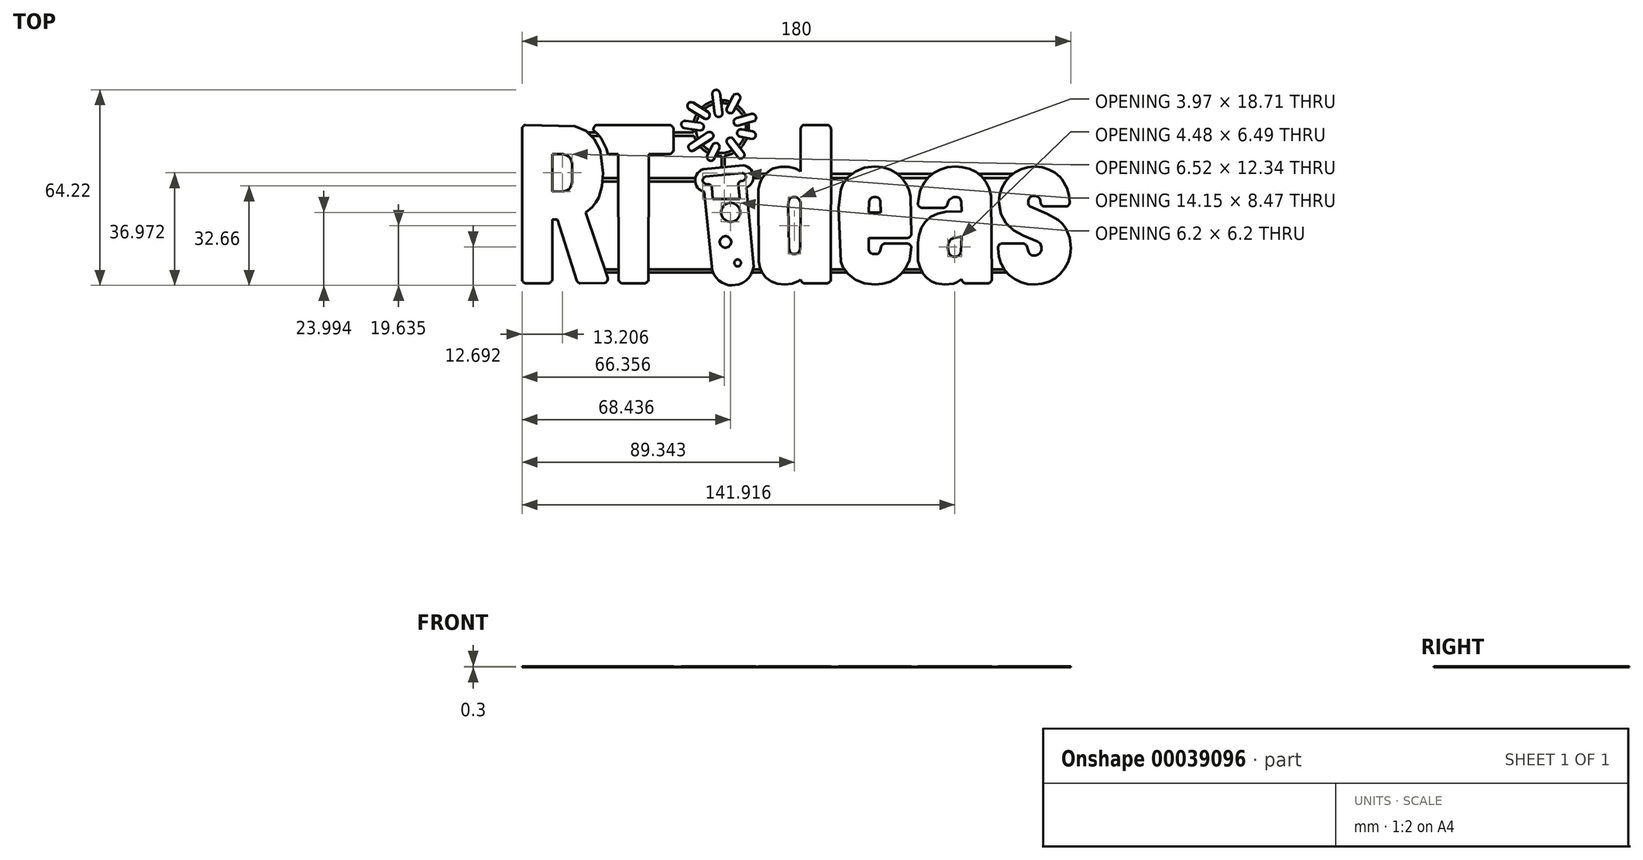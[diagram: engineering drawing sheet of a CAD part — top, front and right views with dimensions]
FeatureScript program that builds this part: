
annotation { "Feature Type Name" : "Feature", "Feature Type Description" : "" }
export const myFeature = defineFeature(function(context is Context, id is Id, definition is map)
    precondition{}
    {
        {
            var Q0;
            Q0=qCreatedBy(makeId("Top.planeOp"),FACE);
            var sketch = newSketch(context, id + "F0", { "sketchPlane" : qUnion([Q0])});
            skLineSegment(sketch, "E0", {"start": v(-21.05, -32.1) * mm, "end": v(-22.22, -32) * mm});
            skLineSegment(sketch, "E1", {"start": v(-22.22, -32) * mm, "end": v(-23.33, -31.71) * mm});
            skLineSegment(sketch, "E2", {"start": v(-23.33, -31.71) * mm, "end": v(-24.38, -31.22) * mm});
            skLineSegment(sketch, "E3", {"start": v(-24.38, -31.22) * mm, "end": v(-25.36, -30.53) * mm});
            skLineSegment(sketch, "E4", {"start": v(-25.36, -30.53) * mm, "end": v(-26.34, -29.57) * mm});
            skLineSegment(sketch, "E5", {"start": v(-26.34, -29.57) * mm, "end": v(-27.07, -28.47) * mm});
            skLineSegment(sketch, "E6", {"start": v(-27.07, -28.47) * mm, "end": v(-27.57, -27.24) * mm});
            skLineSegment(sketch, "E7", {"start": v(-27.57, -27.24) * mm, "end": v(-30.18, -1.33) * mm});
            skLineSegment(sketch, "E8", {"start": v(-30.18, -1.33) * mm, "end": v(-31.06, -1.04) * mm});
            skLineSegment(sketch, "E9", {"start": v(-31.06, -1.04) * mm, "end": v(-31.86, -0.53) * mm});
            skLineSegment(sketch, "E10", {"start": v(-31.86, -0.53) * mm, "end": v(-32.4, 0) * mm});
            skLineSegment(sketch, "E11", {"start": v(-32.4, 0) * mm, "end": v(-32.8, 0.61) * mm});
            skLineSegment(sketch, "E12", {"start": v(-32.8, 0.61) * mm, "end": v(-33.07, 1.3) * mm});
            skLineSegment(sketch, "E13", {"start": v(-33.07, 1.3) * mm, "end": v(-33.22, 2.03) * mm});
            skLineSegment(sketch, "E14", {"start": v(-33.22, 2.03) * mm, "end": v(-33.22, 2.79) * mm});
            skLineSegment(sketch, "E15", {"start": v(-33.22, 2.79) * mm, "end": v(-33.08, 3.5) * mm});
            skLineSegment(sketch, "E16", {"start": v(-33.08, 3.5) * mm, "end": v(-32.8, 4.18) * mm});
            skLineSegment(sketch, "E17", {"start": v(-32.8, 4.18) * mm, "end": v(-32.37, 4.8) * mm});
            skLineSegment(sketch, "E18", {"start": v(-32.37, 4.8) * mm, "end": v(-31.84, 5.34) * mm});
            skLineSegment(sketch, "E19", {"start": v(-31.84, 5.34) * mm, "end": v(-31.22, 5.75) * mm});
            skLineSegment(sketch, "E20", {"start": v(-31.22, 5.75) * mm, "end": v(-30.54, 6.03) * mm});
            skLineSegment(sketch, "E21", {"start": v(-30.54, 6.03) * mm, "end": v(-17.45, 7.28) * mm});
            skLineSegment(sketch, "E22", {"start": v(-17.45, 7.28) * mm, "end": v(-16.73, 7.14) * mm});
            skLineSegment(sketch, "E23", {"start": v(-16.73, 7.14) * mm, "end": v(-16.06, 6.86) * mm});
            skLineSegment(sketch, "E24", {"start": v(-16.06, 6.86) * mm, "end": v(-15.43, 6.44) * mm});
            skLineSegment(sketch, "E25", {"start": v(-15.43, 6.44) * mm, "end": v(-14.9, 5.9) * mm});
            skLineSegment(sketch, "E26", {"start": v(-14.9, 5.9) * mm, "end": v(-14.5, 5.3) * mm});
            skLineSegment(sketch, "E27", {"start": v(-14.5, 5.3) * mm, "end": v(-14.21, 4.61) * mm});
            skLineSegment(sketch, "E28", {"start": v(-14.21, 4.61) * mm, "end": v(-14.07, 3.87) * mm});
            skLineSegment(sketch, "E29", {"start": v(-14.07, 3.87) * mm, "end": v(-14.07, 3.12) * mm});
            skLineSegment(sketch, "E30", {"start": v(-14.07, 3.12) * mm, "end": v(-14.22, 2.4) * mm});
            skLineSegment(sketch, "E31", {"start": v(-14.22, 2.4) * mm, "end": v(-14.5, 1.72) * mm});
            skLineSegment(sketch, "E32", {"start": v(-14.5, 1.72) * mm, "end": v(-15.25, 0.75) * mm});
            skLineSegment(sketch, "E33", {"start": v(-15.25, 0.75) * mm, "end": v(-16, 0.2) * mm});
            skLineSegment(sketch, "E34", {"start": v(-16, 0.2) * mm, "end": v(-16.4, 0) * mm});
            skLineSegment(sketch, "E35", {"start": v(-16.4, 0) * mm, "end": v(-14.05, -25.94) * mm});
            skLineSegment(sketch, "E36", {"start": v(-14.05, -25.94) * mm, "end": v(-14.3, -27.24) * mm});
            skLineSegment(sketch, "E37", {"start": v(-14.3, -27.24) * mm, "end": v(-14.82, -28.46) * mm});
            skLineSegment(sketch, "E38", {"start": v(-14.82, -28.46) * mm, "end": v(-15.6, -29.6) * mm});
            skLineSegment(sketch, "E39", {"start": v(-15.6, -29.6) * mm, "end": v(-16.56, -30.57) * mm});
            skLineSegment(sketch, "E40", {"start": v(-16.56, -30.57) * mm, "end": v(-17.66, -31.31) * mm});
            skLineSegment(sketch, "E41", {"start": v(-17.66, -31.31) * mm, "end": v(-18.89, -31.8) * mm});
            skLineSegment(sketch, "E42", {"start": v(-18.89, -31.8) * mm, "end": v(-21.05, -32.1) * mm});
            skLineSegment(sketch, "E43", {"start": v(-18.14, -24.6) * mm, "end": v(-18.18, -24.38) * mm});
            skLineSegment(sketch, "E44", {"start": v(-18.18, -24.38) * mm, "end": v(-18.26, -24.18) * mm});
            skLineSegment(sketch, "E45", {"start": v(-18.26, -24.18) * mm, "end": v(-18.38, -24) * mm});
            skLineSegment(sketch, "E46", {"start": v(-18.38, -24) * mm, "end": v(-18.54, -23.84) * mm});
            skLineSegment(sketch, "E47", {"start": v(-18.54, -23.84) * mm, "end": v(-18.73, -23.71) * mm});
            skLineSegment(sketch, "E48", {"start": v(-18.73, -23.71) * mm, "end": v(-18.93, -23.63) * mm});
            skLineSegment(sketch, "E49", {"start": v(-18.93, -23.63) * mm, "end": v(-19.15, -23.59) * mm});
            skLineSegment(sketch, "E50", {"start": v(-19.15, -23.59) * mm, "end": v(-19.37, -23.59) * mm});
            skLineSegment(sketch, "E51", {"start": v(-19.37, -23.59) * mm, "end": v(-19.6, -23.63) * mm});
            skLineSegment(sketch, "E52", {"start": v(-19.6, -23.63) * mm, "end": v(-19.8, -23.71) * mm});
            skLineSegment(sketch, "E53", {"start": v(-19.8, -23.71) * mm, "end": v(-19.98, -23.83) * mm});
            skLineSegment(sketch, "E54", {"start": v(-19.98, -23.83) * mm, "end": v(-20.14, -24) * mm});
            skLineSegment(sketch, "E55", {"start": v(-20.14, -24) * mm, "end": v(-20.26, -24.18) * mm});
            skLineSegment(sketch, "E56", {"start": v(-20.26, -24.18) * mm, "end": v(-20.35, -24.38) * mm});
            skLineSegment(sketch, "E57", {"start": v(-20.35, -24.38) * mm, "end": v(-20.39, -24.6) * mm});
            skLineSegment(sketch, "E58", {"start": v(-20.39, -24.6) * mm, "end": v(-20.39, -24.82) * mm});
            skLineSegment(sketch, "E59", {"start": v(-20.39, -24.82) * mm, "end": v(-20.35, -25.04) * mm});
            skLineSegment(sketch, "E60", {"start": v(-20.35, -25.04) * mm, "end": v(-20.27, -25.24) * mm});
            skLineSegment(sketch, "E61", {"start": v(-20.27, -25.24) * mm, "end": v(-20.14, -25.43) * mm});
            skLineSegment(sketch, "E62", {"start": v(-20.14, -25.43) * mm, "end": v(-19.98, -25.58) * mm});
            skLineSegment(sketch, "E63", {"start": v(-19.98, -25.58) * mm, "end": v(-19.8, -25.71) * mm});
            skLineSegment(sketch, "E64", {"start": v(-19.8, -25.71) * mm, "end": v(-19.6, -25.8) * mm});
            skLineSegment(sketch, "E65", {"start": v(-19.6, -25.8) * mm, "end": v(-19.38, -25.84) * mm});
            skLineSegment(sketch, "E66", {"start": v(-19.38, -25.84) * mm, "end": v(-19.16, -25.84) * mm});
            skLineSegment(sketch, "E67", {"start": v(-19.16, -25.84) * mm, "end": v(-18.93, -25.8) * mm});
            skLineSegment(sketch, "E68", {"start": v(-18.93, -25.8) * mm, "end": v(-18.73, -25.71) * mm});
            skLineSegment(sketch, "E69", {"start": v(-18.73, -25.71) * mm, "end": v(-18.55, -25.6) * mm});
            skLineSegment(sketch, "E70", {"start": v(-18.55, -25.6) * mm, "end": v(-18.4, -25.43) * mm});
            skLineSegment(sketch, "E71", {"start": v(-18.4, -25.43) * mm, "end": v(-18.26, -25.24) * mm});
            skLineSegment(sketch, "E72", {"start": v(-18.26, -25.24) * mm, "end": v(-18.18, -25.04) * mm});
            skLineSegment(sketch, "E73", {"start": v(-18.18, -25.04) * mm, "end": v(-18.14, -24.83) * mm});
            skLineSegment(sketch, "E74", {"start": v(-18.14, -24.83) * mm, "end": v(-18.14, -24.6) * mm});
            skLineSegment(sketch, "E75", {"start": v(-21.4, -17.66) * mm, "end": v(-21.48, -17.3) * mm});
            skLineSegment(sketch, "E76", {"start": v(-21.48, -17.3) * mm, "end": v(-21.61, -16.96) * mm});
            skLineSegment(sketch, "E77", {"start": v(-21.61, -16.96) * mm, "end": v(-21.81, -16.66) * mm});
            skLineSegment(sketch, "E78", {"start": v(-21.81, -16.66) * mm, "end": v(-22.08, -16.4) * mm});
            skLineSegment(sketch, "E79", {"start": v(-22.08, -16.4) * mm, "end": v(-22.39, -16.18) * mm});
            skLineSegment(sketch, "E80", {"start": v(-22.39, -16.18) * mm, "end": v(-22.72, -16.04) * mm});
            skLineSegment(sketch, "E81", {"start": v(-22.72, -16.04) * mm, "end": v(-23.07, -15.97) * mm});
            skLineSegment(sketch, "E82", {"start": v(-23.07, -15.97) * mm, "end": v(-23.45, -15.98) * mm});
            skLineSegment(sketch, "E83", {"start": v(-23.45, -15.98) * mm, "end": v(-23.82, -16.05) * mm});
            skLineSegment(sketch, "E84", {"start": v(-23.82, -16.05) * mm, "end": v(-24.15, -16.18) * mm});
            skLineSegment(sketch, "E85", {"start": v(-24.15, -16.18) * mm, "end": v(-24.45, -16.38) * mm});
            skLineSegment(sketch, "E86", {"start": v(-24.45, -16.38) * mm, "end": v(-24.72, -16.65) * mm});
            skLineSegment(sketch, "E87", {"start": v(-24.72, -16.65) * mm, "end": v(-24.93, -16.96) * mm});
            skLineSegment(sketch, "E88", {"start": v(-24.93, -16.96) * mm, "end": v(-25.07, -17.29) * mm});
            skLineSegment(sketch, "E89", {"start": v(-25.07, -17.29) * mm, "end": v(-25.14, -17.64) * mm});
            skLineSegment(sketch, "E90", {"start": v(-25.14, -17.64) * mm, "end": v(-25.13, -18.02) * mm});
            skLineSegment(sketch, "E91", {"start": v(-25.13, -18.02) * mm, "end": v(-25.07, -18.39) * mm});
            skLineSegment(sketch, "E92", {"start": v(-25.07, -18.39) * mm, "end": v(-24.93, -18.72) * mm});
            skLineSegment(sketch, "E93", {"start": v(-24.93, -18.72) * mm, "end": v(-24.73, -19.02) * mm});
            skLineSegment(sketch, "E94", {"start": v(-24.73, -19.02) * mm, "end": v(-24.46, -19.28) * mm});
            skLineSegment(sketch, "E95", {"start": v(-24.46, -19.28) * mm, "end": v(-24.15, -19.5) * mm});
            skLineSegment(sketch, "E96", {"start": v(-24.15, -19.5) * mm, "end": v(-23.82, -19.64) * mm});
            skLineSegment(sketch, "E97", {"start": v(-23.82, -19.64) * mm, "end": v(-23.47, -19.7) * mm});
            skLineSegment(sketch, "E98", {"start": v(-23.47, -19.7) * mm, "end": v(-23.1, -19.7) * mm});
            skLineSegment(sketch, "E99", {"start": v(-23.1, -19.7) * mm, "end": v(-22.72, -19.63) * mm});
            skLineSegment(sketch, "E100", {"start": v(-22.72, -19.63) * mm, "end": v(-22.39, -19.5) * mm});
            skLineSegment(sketch, "E101", {"start": v(-22.39, -19.5) * mm, "end": v(-22.1, -19.3) * mm});
            skLineSegment(sketch, "E102", {"start": v(-22.1, -19.3) * mm, "end": v(-21.83, -19.03) * mm});
            skLineSegment(sketch, "E103", {"start": v(-21.83, -19.03) * mm, "end": v(-21.62, -18.72) * mm});
            skLineSegment(sketch, "E104", {"start": v(-21.62, -18.72) * mm, "end": v(-21.47, -18.4) * mm});
            skLineSegment(sketch, "E105", {"start": v(-21.47, -18.4) * mm, "end": v(-21.4, -18.04) * mm});
            skLineSegment(sketch, "E106", {"start": v(-21.4, -18.04) * mm, "end": v(-21.4, -17.66) * mm});
            skLineSegment(sketch, "E107", {"start": v(-18.47, -7.82) * mm, "end": v(-18.58, -7.2) * mm});
            skLineSegment(sketch, "E108", {"start": v(-18.58, -7.2) * mm, "end": v(-18.8, -6.65) * mm});
            skLineSegment(sketch, "E109", {"start": v(-18.8, -6.65) * mm, "end": v(-19.14, -6.15) * mm});
            skLineSegment(sketch, "E110", {"start": v(-19.14, -6.15) * mm, "end": v(-19.58, -5.72) * mm});
            skLineSegment(sketch, "E111", {"start": v(-19.58, -5.72) * mm, "end": v(-20.1, -5.36) * mm});
            skLineSegment(sketch, "E112", {"start": v(-20.1, -5.36) * mm, "end": v(-20.65, -5.13) * mm});
            skLineSegment(sketch, "E113", {"start": v(-20.65, -5.13) * mm, "end": v(-21.24, -5.02) * mm});
            skLineSegment(sketch, "E114", {"start": v(-21.24, -5.02) * mm, "end": v(-21.86, -5.02) * mm});
            skLineSegment(sketch, "E115", {"start": v(-21.86, -5.02) * mm, "end": v(-22.47, -5.13) * mm});
            skLineSegment(sketch, "E116", {"start": v(-22.47, -5.13) * mm, "end": v(-23.03, -5.36) * mm});
            skLineSegment(sketch, "E117", {"start": v(-23.03, -5.36) * mm, "end": v(-23.52, -5.7) * mm});
            skLineSegment(sketch, "E118", {"start": v(-23.52, -5.7) * mm, "end": v(-23.96, -6.14) * mm});
            skLineSegment(sketch, "E119", {"start": v(-23.96, -6.14) * mm, "end": v(-24.31, -6.65) * mm});
            skLineSegment(sketch, "E120", {"start": v(-24.31, -6.65) * mm, "end": v(-24.55, -7.2) * mm});
            skLineSegment(sketch, "E121", {"start": v(-24.55, -7.2) * mm, "end": v(-24.66, -7.79) * mm});
            skLineSegment(sketch, "E122", {"start": v(-24.66, -7.79) * mm, "end": v(-24.66, -8.41) * mm});
            skLineSegment(sketch, "E123", {"start": v(-24.66, -8.41) * mm, "end": v(-24.55, -9.02) * mm});
            skLineSegment(sketch, "E124", {"start": v(-24.55, -9.02) * mm, "end": v(-24.32, -9.58) * mm});
            skLineSegment(sketch, "E125", {"start": v(-24.32, -9.58) * mm, "end": v(-23.99, -10.08) * mm});
            skLineSegment(sketch, "E126", {"start": v(-23.99, -10.08) * mm, "end": v(-23.54, -10.52) * mm});
            skLineSegment(sketch, "E127", {"start": v(-23.54, -10.52) * mm, "end": v(-23.03, -10.87) * mm});
            skLineSegment(sketch, "E128", {"start": v(-23.03, -10.87) * mm, "end": v(-22.48, -11.1) * mm});
            skLineSegment(sketch, "E129", {"start": v(-22.48, -11.1) * mm, "end": v(-21.9, -11.21) * mm});
            skLineSegment(sketch, "E130", {"start": v(-21.9, -11.21) * mm, "end": v(-21.27, -11.21) * mm});
            skLineSegment(sketch, "E131", {"start": v(-21.27, -11.21) * mm, "end": v(-20.65, -11.1) * mm});
            skLineSegment(sketch, "E132", {"start": v(-20.65, -11.1) * mm, "end": v(-20.1, -10.87) * mm});
            skLineSegment(sketch, "E133", {"start": v(-20.1, -10.87) * mm, "end": v(-19.6, -10.54) * mm});
            skLineSegment(sketch, "E134", {"start": v(-19.6, -10.54) * mm, "end": v(-19.16, -10.1) * mm});
            skLineSegment(sketch, "E135", {"start": v(-19.16, -10.1) * mm, "end": v(-18.81, -9.58) * mm});
            skLineSegment(sketch, "E136", {"start": v(-18.81, -9.58) * mm, "end": v(-18.58, -9.03) * mm});
            skLineSegment(sketch, "E137", {"start": v(-18.58, -9.03) * mm, "end": v(-18.47, -8.44) * mm});
            skLineSegment(sketch, "E138", {"start": v(-18.47, -8.44) * mm, "end": v(-18.47, -7.82) * mm});
            skLineSegment(sketch, "E139", {"start": v(-28.07, 8.75) * mm, "end": v(-28.34, 8.79) * mm});
            skLineSegment(sketch, "E140", {"start": v(-28.34, 8.79) * mm, "end": v(-28.6, 8.88) * mm});
            skLineSegment(sketch, "E141", {"start": v(-28.6, 8.88) * mm, "end": v(-29, 9.18) * mm});
            skLineSegment(sketch, "E142", {"start": v(-29, 9.18) * mm, "end": v(-29.25, 9.6) * mm});
            skLineSegment(sketch, "E143", {"start": v(-29.25, 9.6) * mm, "end": v(-29.32, 10.07) * mm});
            skLineSegment(sketch, "E144", {"start": v(-29.32, 10.07) * mm, "end": v(-29.2, 10.55) * mm});
            skLineSegment(sketch, "E145", {"start": v(-29.2, 10.55) * mm, "end": v(-27.57, 13.96) * mm});
            skLineSegment(sketch, "E146", {"start": v(-27.57, 13.96) * mm, "end": v(-27.27, 14.36) * mm});
            skLineSegment(sketch, "E147", {"start": v(-27.27, 14.36) * mm, "end": v(-26.85, 14.6) * mm});
            skLineSegment(sketch, "E148", {"start": v(-26.85, 14.6) * mm, "end": v(-26.38, 14.67) * mm});
            skLineSegment(sketch, "E149", {"start": v(-26.38, 14.67) * mm, "end": v(-25.9, 14.55) * mm});
            skLineSegment(sketch, "E150", {"start": v(-25.9, 14.55) * mm, "end": v(-25.5, 14.25) * mm});
            skLineSegment(sketch, "E151", {"start": v(-25.5, 14.25) * mm, "end": v(-25.25, 13.84) * mm});
            skLineSegment(sketch, "E152", {"start": v(-25.25, 13.84) * mm, "end": v(-25.18, 13.36) * mm});
            skLineSegment(sketch, "E153", {"start": v(-25.18, 13.36) * mm, "end": v(-25.3, 12.88) * mm});
            skLineSegment(sketch, "E154", {"start": v(-25.3, 12.88) * mm, "end": v(-27.14, 9.17) * mm});
            skLineSegment(sketch, "E155", {"start": v(-27.14, 9.17) * mm, "end": v(-27.4, 8.94) * mm});
            skLineSegment(sketch, "E156", {"start": v(-27.4, 8.94) * mm, "end": v(-27.72, 8.8) * mm});
            skLineSegment(sketch, "E157", {"start": v(-27.72, 8.8) * mm, "end": v(-28.07, 8.75) * mm});
            skLineSegment(sketch, "E158", {"start": v(-18.27, 9.53) * mm, "end": v(-18.55, 9.56) * mm});
            skLineSegment(sketch, "E159", {"start": v(-18.55, 9.56) * mm, "end": v(-18.82, 9.65) * mm});
            skLineSegment(sketch, "E160", {"start": v(-18.82, 9.65) * mm, "end": v(-19.06, 9.8) * mm});
            skLineSegment(sketch, "E161", {"start": v(-19.06, 9.8) * mm, "end": v(-22.66, 14.41) * mm});
            skLineSegment(sketch, "E162", {"start": v(-22.66, 14.41) * mm, "end": v(-22.88, 14.86) * mm});
            skLineSegment(sketch, "E163", {"start": v(-22.88, 14.86) * mm, "end": v(-22.9, 15.34) * mm});
            skLineSegment(sketch, "E164", {"start": v(-22.9, 15.34) * mm, "end": v(-22.76, 15.8) * mm});
            skLineSegment(sketch, "E165", {"start": v(-22.76, 15.8) * mm, "end": v(-22.43, 16.17) * mm});
            skLineSegment(sketch, "E166", {"start": v(-22.43, 16.17) * mm, "end": v(-21.98, 16.4) * mm});
            skLineSegment(sketch, "E167", {"start": v(-21.98, 16.4) * mm, "end": v(-21.5, 16.42) * mm});
            skLineSegment(sketch, "E168", {"start": v(-21.5, 16.42) * mm, "end": v(-21.05, 16.27) * mm});
            skLineSegment(sketch, "E169", {"start": v(-21.05, 16.27) * mm, "end": v(-20.67, 15.95) * mm});
            skLineSegment(sketch, "E170", {"start": v(-20.67, 15.95) * mm, "end": v(-17.28, 11.55) * mm});
            skLineSegment(sketch, "E171", {"start": v(-17.28, 11.55) * mm, "end": v(-17.06, 11.1) * mm});
            skLineSegment(sketch, "E172", {"start": v(-17.06, 11.1) * mm, "end": v(-17.03, 10.62) * mm});
            skLineSegment(sketch, "E173", {"start": v(-17.03, 10.62) * mm, "end": v(-17.18, 10.17) * mm});
            skLineSegment(sketch, "E174", {"start": v(-17.18, 10.17) * mm, "end": v(-17.5, 9.79) * mm});
            skLineSegment(sketch, "E175", {"start": v(-17.5, 9.79) * mm, "end": v(-17.68, 9.67) * mm});
            skLineSegment(sketch, "E176", {"start": v(-17.68, 9.67) * mm, "end": v(-17.87, 9.6) * mm});
            skLineSegment(sketch, "E177", {"start": v(-17.87, 9.6) * mm, "end": v(-18.07, 9.54) * mm});
            skLineSegment(sketch, "E178", {"start": v(-18.07, 9.54) * mm, "end": v(-18.27, 9.53) * mm});
            skLineSegment(sketch, "E179", {"start": v(-34.18, 12.03) * mm, "end": v(-34.48, 12.07) * mm});
            skLineSegment(sketch, "E180", {"start": v(-34.48, 12.07) * mm, "end": v(-34.77, 12.18) * mm});
            skLineSegment(sketch, "E181", {"start": v(-34.77, 12.18) * mm, "end": v(-35.02, 12.35) * mm});
            skLineSegment(sketch, "E182", {"start": v(-35.02, 12.35) * mm, "end": v(-35.23, 12.6) * mm});
            skLineSegment(sketch, "E183", {"start": v(-35.23, 12.6) * mm, "end": v(-35.42, 13.06) * mm});
            skLineSegment(sketch, "E184", {"start": v(-35.42, 13.06) * mm, "end": v(-35.41, 13.54) * mm});
            skLineSegment(sketch, "E185", {"start": v(-35.41, 13.54) * mm, "end": v(-35.23, 13.99) * mm});
            skLineSegment(sketch, "E186", {"start": v(-35.23, 13.99) * mm, "end": v(-34.87, 14.34) * mm});
            skLineSegment(sketch, "E187", {"start": v(-34.87, 14.34) * mm, "end": v(-29.19, 18.09) * mm});
            skLineSegment(sketch, "E188", {"start": v(-29.19, 18.09) * mm, "end": v(-28.72, 18.27) * mm});
            skLineSegment(sketch, "E189", {"start": v(-28.72, 18.27) * mm, "end": v(-28.24, 18.27) * mm});
            skLineSegment(sketch, "E190", {"start": v(-28.24, 18.27) * mm, "end": v(-27.8, 18.08) * mm});
            skLineSegment(sketch, "E191", {"start": v(-27.8, 18.08) * mm, "end": v(-27.45, 17.73) * mm});
            skLineSegment(sketch, "E192", {"start": v(-27.45, 17.73) * mm, "end": v(-27.26, 17.27) * mm});
            skLineSegment(sketch, "E193", {"start": v(-27.26, 17.27) * mm, "end": v(-27.26, 16.78) * mm});
            skLineSegment(sketch, "E194", {"start": v(-27.26, 16.78) * mm, "end": v(-27.45, 16.34) * mm});
            skLineSegment(sketch, "E195", {"start": v(-27.45, 16.34) * mm, "end": v(-27.8, 15.99) * mm});
            skLineSegment(sketch, "E196", {"start": v(-27.8, 15.99) * mm, "end": v(-33.83, 12.08) * mm});
            skLineSegment(sketch, "E197", {"start": v(-33.83, 12.08) * mm, "end": v(-34.18, 12.03) * mm});
            skLineSegment(sketch, "E198", {"start": v(-14.6, 15.98) * mm, "end": v(-18.41, 16.7) * mm});
            skLineSegment(sketch, "E199", {"start": v(-18.41, 16.7) * mm, "end": v(-18.87, 16.9) * mm});
            skLineSegment(sketch, "E200", {"start": v(-18.87, 16.9) * mm, "end": v(-19.21, 17.24) * mm});
            skLineSegment(sketch, "E201", {"start": v(-19.21, 17.24) * mm, "end": v(-19.4, 17.69) * mm});
            skLineSegment(sketch, "E202", {"start": v(-19.4, 17.69) * mm, "end": v(-19.4, 18.19) * mm});
            skLineSegment(sketch, "E203", {"start": v(-19.4, 18.19) * mm, "end": v(-19.2, 18.65) * mm});
            skLineSegment(sketch, "E204", {"start": v(-19.2, 18.65) * mm, "end": v(-18.86, 18.99) * mm});
            skLineSegment(sketch, "E205", {"start": v(-18.86, 18.99) * mm, "end": v(-18.42, 19.17) * mm});
            skLineSegment(sketch, "E206", {"start": v(-18.42, 19.17) * mm, "end": v(-17.92, 19.17) * mm});
            skLineSegment(sketch, "E207", {"start": v(-17.92, 19.17) * mm, "end": v(-14.36, 18.46) * mm});
            skLineSegment(sketch, "E208", {"start": v(-14.36, 18.46) * mm, "end": v(-13.9, 18.27) * mm});
            skLineSegment(sketch, "E209", {"start": v(-13.9, 18.27) * mm, "end": v(-13.56, 17.93) * mm});
            skLineSegment(sketch, "E210", {"start": v(-13.56, 17.93) * mm, "end": v(-13.38, 17.48) * mm});
            skLineSegment(sketch, "E211", {"start": v(-13.38, 17.48) * mm, "end": v(-13.37, 16.99) * mm});
            skLineSegment(sketch, "E212", {"start": v(-13.37, 16.99) * mm, "end": v(-13.53, 16.58) * mm});
            skLineSegment(sketch, "E213", {"start": v(-13.53, 16.58) * mm, "end": v(-13.81, 16.26) * mm});
            skLineSegment(sketch, "E214", {"start": v(-13.81, 16.26) * mm, "end": v(-14.18, 16.05) * mm});
            skLineSegment(sketch, "E215", {"start": v(-14.18, 16.05) * mm, "end": v(-14.6, 15.98) * mm});
            skLineSegment(sketch, "E216", {"start": v(-31.6, 18.76) * mm, "end": v(-36.7, 19.47) * mm});
            skLineSegment(sketch, "E217", {"start": v(-36.7, 19.47) * mm, "end": v(-37.16, 19.63) * mm});
            skLineSegment(sketch, "E218", {"start": v(-37.16, 19.63) * mm, "end": v(-37.52, 19.96) * mm});
            skLineSegment(sketch, "E219", {"start": v(-37.52, 19.96) * mm, "end": v(-37.73, 20.39) * mm});
            skLineSegment(sketch, "E220", {"start": v(-37.73, 20.39) * mm, "end": v(-37.76, 20.89) * mm});
            skLineSegment(sketch, "E221", {"start": v(-37.76, 20.89) * mm, "end": v(-37.6, 21.36) * mm});
            skLineSegment(sketch, "E222", {"start": v(-37.6, 21.36) * mm, "end": v(-37.27, 21.71) * mm});
            skLineSegment(sketch, "E223", {"start": v(-37.27, 21.71) * mm, "end": v(-36.84, 21.92) * mm});
            skLineSegment(sketch, "E224", {"start": v(-36.84, 21.92) * mm, "end": v(-36.34, 21.95) * mm});
            skLineSegment(sketch, "E225", {"start": v(-36.34, 21.95) * mm, "end": v(-31.42, 21.26) * mm});
            skLineSegment(sketch, "E226", {"start": v(-31.42, 21.26) * mm, "end": v(-30.95, 21.1) * mm});
            skLineSegment(sketch, "E227", {"start": v(-30.95, 21.1) * mm, "end": v(-30.6, 20.77) * mm});
            skLineSegment(sketch, "E228", {"start": v(-30.6, 20.77) * mm, "end": v(-30.38, 20.33) * mm});
            skLineSegment(sketch, "E229", {"start": v(-30.38, 20.33) * mm, "end": v(-30.35, 19.84) * mm});
            skLineSegment(sketch, "E230", {"start": v(-30.35, 19.84) * mm, "end": v(-30.5, 19.4) * mm});
            skLineSegment(sketch, "E231", {"start": v(-30.5, 19.4) * mm, "end": v(-30.78, 19.06) * mm});
            skLineSegment(sketch, "E232", {"start": v(-30.78, 19.06) * mm, "end": v(-31.15, 18.84) * mm});
            skLineSegment(sketch, "E233", {"start": v(-31.15, 18.84) * mm, "end": v(-31.6, 18.76) * mm});
            skLineSegment(sketch, "E234", {"start": v(-19.32, 20.3) * mm, "end": v(-19.72, 20.37) * mm});
            skLineSegment(sketch, "E235", {"start": v(-19.72, 20.37) * mm, "end": v(-20.07, 20.55) * mm});
            skLineSegment(sketch, "E236", {"start": v(-20.07, 20.55) * mm, "end": v(-20.35, 20.84) * mm});
            skLineSegment(sketch, "E237", {"start": v(-20.35, 20.84) * mm, "end": v(-20.53, 21.22) * mm});
            skLineSegment(sketch, "E238", {"start": v(-20.53, 21.22) * mm, "end": v(-20.57, 21.71) * mm});
            skLineSegment(sketch, "E239", {"start": v(-20.57, 21.71) * mm, "end": v(-20.42, 22.17) * mm});
            skLineSegment(sketch, "E240", {"start": v(-20.42, 22.17) * mm, "end": v(-20.1, 22.54) * mm});
            skLineSegment(sketch, "E241", {"start": v(-20.1, 22.54) * mm, "end": v(-19.66, 22.77) * mm});
            skLineSegment(sketch, "E242", {"start": v(-19.66, 22.77) * mm, "end": v(-14.78, 24.15) * mm});
            skLineSegment(sketch, "E243", {"start": v(-14.78, 24.15) * mm, "end": v(-14.28, 24.19) * mm});
            skLineSegment(sketch, "E244", {"start": v(-14.28, 24.19) * mm, "end": v(-13.82, 24.04) * mm});
            skLineSegment(sketch, "E245", {"start": v(-13.82, 24.04) * mm, "end": v(-13.46, 23.72) * mm});
            skLineSegment(sketch, "E246", {"start": v(-13.46, 23.72) * mm, "end": v(-13.23, 23.28) * mm});
            skLineSegment(sketch, "E247", {"start": v(-13.23, 23.28) * mm, "end": v(-13.19, 22.78) * mm});
            skLineSegment(sketch, "E248", {"start": v(-13.19, 22.78) * mm, "end": v(-13.34, 22.33) * mm});
            skLineSegment(sketch, "E249", {"start": v(-13.34, 22.33) * mm, "end": v(-13.65, 21.96) * mm});
            skLineSegment(sketch, "E250", {"start": v(-13.65, 21.96) * mm, "end": v(-14.1, 21.73) * mm});
            skLineSegment(sketch, "E251", {"start": v(-14.1, 21.73) * mm, "end": v(-19.32, 20.3) * mm});
            skLineSegment(sketch, "E252", {"start": v(-29.66, 22.5) * mm, "end": v(-30, 22.55) * mm});
            skLineSegment(sketch, "E253", {"start": v(-30, 22.55) * mm, "end": v(-35.2, 25.78) * mm});
            skLineSegment(sketch, "E254", {"start": v(-35.2, 25.78) * mm, "end": v(-35.57, 26.12) * mm});
            skLineSegment(sketch, "E255", {"start": v(-35.57, 26.12) * mm, "end": v(-35.76, 26.56) * mm});
            skLineSegment(sketch, "E256", {"start": v(-35.76, 26.56) * mm, "end": v(-35.77, 27.04) * mm});
            skLineSegment(sketch, "E257", {"start": v(-35.77, 27.04) * mm, "end": v(-35.6, 27.5) * mm});
            skLineSegment(sketch, "E258", {"start": v(-35.6, 27.5) * mm, "end": v(-35.25, 27.87) * mm});
            skLineSegment(sketch, "E259", {"start": v(-35.25, 27.87) * mm, "end": v(-34.81, 28.06) * mm});
            skLineSegment(sketch, "E260", {"start": v(-34.81, 28.06) * mm, "end": v(-34.33, 28.08) * mm});
            skLineSegment(sketch, "E261", {"start": v(-34.33, 28.08) * mm, "end": v(-33.86, 27.9) * mm});
            skLineSegment(sketch, "E262", {"start": v(-33.86, 27.9) * mm, "end": v(-29, 24.82) * mm});
            skLineSegment(sketch, "E263", {"start": v(-29, 24.82) * mm, "end": v(-28.63, 24.48) * mm});
            skLineSegment(sketch, "E264", {"start": v(-28.63, 24.48) * mm, "end": v(-28.44, 24.04) * mm});
            skLineSegment(sketch, "E265", {"start": v(-28.44, 24.04) * mm, "end": v(-28.42, 23.56) * mm});
            skLineSegment(sketch, "E266", {"start": v(-28.42, 23.56) * mm, "end": v(-28.6, 23.1) * mm});
            skLineSegment(sketch, "E267", {"start": v(-28.6, 23.1) * mm, "end": v(-28.8, 22.84) * mm});
            skLineSegment(sketch, "E268", {"start": v(-28.8, 22.84) * mm, "end": v(-29.07, 22.66) * mm});
            skLineSegment(sketch, "E269", {"start": v(-29.07, 22.66) * mm, "end": v(-29.36, 22.54) * mm});
            skLineSegment(sketch, "E270", {"start": v(-29.36, 22.54) * mm, "end": v(-29.66, 22.5) * mm});
            skLineSegment(sketch, "E271", {"start": v(-25.53, 23.15) * mm, "end": v(-25.97, 23.23) * mm});
            skLineSegment(sketch, "E272", {"start": v(-25.97, 23.23) * mm, "end": v(-26.35, 23.46) * mm});
            skLineSegment(sketch, "E273", {"start": v(-26.35, 23.46) * mm, "end": v(-26.63, 23.8) * mm});
            skLineSegment(sketch, "E274", {"start": v(-26.63, 23.8) * mm, "end": v(-26.77, 24.24) * mm});
            skLineSegment(sketch, "E275", {"start": v(-26.77, 24.24) * mm, "end": v(-27.59, 30.7) * mm});
            skLineSegment(sketch, "E276", {"start": v(-27.59, 30.7) * mm, "end": v(-27.55, 31.2) * mm});
            skLineSegment(sketch, "E277", {"start": v(-27.55, 31.2) * mm, "end": v(-27.33, 31.63) * mm});
            skLineSegment(sketch, "E278", {"start": v(-27.33, 31.63) * mm, "end": v(-26.97, 31.95) * mm});
            skLineSegment(sketch, "E279", {"start": v(-26.97, 31.95) * mm, "end": v(-26.5, 32.1) * mm});
            skLineSegment(sketch, "E280", {"start": v(-26.5, 32.1) * mm, "end": v(-26, 32.07) * mm});
            skLineSegment(sketch, "E281", {"start": v(-26, 32.07) * mm, "end": v(-25.57, 31.86) * mm});
            skLineSegment(sketch, "E282", {"start": v(-25.57, 31.86) * mm, "end": v(-25.25, 31.5) * mm});
            skLineSegment(sketch, "E283", {"start": v(-25.25, 31.5) * mm, "end": v(-25.1, 31.02) * mm});
            skLineSegment(sketch, "E284", {"start": v(-25.1, 31.02) * mm, "end": v(-24.28, 24.56) * mm});
            skLineSegment(sketch, "E285", {"start": v(-24.28, 24.56) * mm, "end": v(-24.32, 24.06) * mm});
            skLineSegment(sketch, "E286", {"start": v(-24.32, 24.06) * mm, "end": v(-24.53, 23.63) * mm});
            skLineSegment(sketch, "E287", {"start": v(-24.53, 23.63) * mm, "end": v(-24.9, 23.32) * mm});
            skLineSegment(sketch, "E288", {"start": v(-24.9, 23.32) * mm, "end": v(-25.37, 23.16) * mm});
            skLineSegment(sketch, "E289", {"start": v(-25.37, 23.16) * mm, "end": v(-25.53, 23.15) * mm});
            skLineSegment(sketch, "E290", {"start": v(-21.65, 24.44) * mm, "end": v(-21.95, 24.48) * mm});
            skLineSegment(sketch, "E291", {"start": v(-21.95, 24.48) * mm, "end": v(-22.24, 24.58) * mm});
            skLineSegment(sketch, "E292", {"start": v(-22.24, 24.58) * mm, "end": v(-22.62, 24.9) * mm});
            skLineSegment(sketch, "E293", {"start": v(-22.62, 24.9) * mm, "end": v(-22.85, 25.32) * mm});
            skLineSegment(sketch, "E294", {"start": v(-22.85, 25.32) * mm, "end": v(-22.9, 25.8) * mm});
            skLineSegment(sketch, "E295", {"start": v(-22.9, 25.8) * mm, "end": v(-22.76, 26.28) * mm});
            skLineSegment(sketch, "E296", {"start": v(-22.76, 26.28) * mm, "end": v(-20.73, 30.12) * mm});
            skLineSegment(sketch, "E297", {"start": v(-20.73, 30.12) * mm, "end": v(-20.42, 30.51) * mm});
            skLineSegment(sketch, "E298", {"start": v(-20.42, 30.51) * mm, "end": v(-20, 30.74) * mm});
            skLineSegment(sketch, "E299", {"start": v(-20, 30.74) * mm, "end": v(-19.51, 30.79) * mm});
            skLineSegment(sketch, "E300", {"start": v(-19.51, 30.79) * mm, "end": v(-19.04, 30.65) * mm});
            skLineSegment(sketch, "E301", {"start": v(-19.04, 30.65) * mm, "end": v(-18.65, 30.33) * mm});
            skLineSegment(sketch, "E302", {"start": v(-18.65, 30.33) * mm, "end": v(-18.42, 29.9) * mm});
            skLineSegment(sketch, "E303", {"start": v(-18.42, 29.9) * mm, "end": v(-18.37, 29.43) * mm});
            skLineSegment(sketch, "E304", {"start": v(-18.37, 29.43) * mm, "end": v(-18.51, 28.95) * mm});
            skLineSegment(sketch, "E305", {"start": v(-18.51, 28.95) * mm, "end": v(-20.75, 24.82) * mm});
            skLineSegment(sketch, "E306", {"start": v(-20.75, 24.82) * mm, "end": v(-21.01, 24.61) * mm});
            skLineSegment(sketch, "E307", {"start": v(-21.01, 24.61) * mm, "end": v(-21.32, 24.48) * mm});
            skLineSegment(sketch, "E308", {"start": v(-21.32, 24.48) * mm, "end": v(-21.65, 24.44) * mm});
            skLineSegment(sketch, "E309", {"start": v(89.58, -16.45) * mm, "end": v(88.33, -13.35) * mm});
            skLineSegment(sketch, "E310", {"start": v(88.33, -13.35) * mm, "end": v(88.33, -13.37) * mm});
            skLineSegment(sketch, "E311", {"start": v(88.33, -13.37) * mm, "end": v(87.27, -11.88) * mm});
            skLineSegment(sketch, "E312", {"start": v(87.27, -11.88) * mm, "end": v(85.83, -10.56) * mm});
            skLineSegment(sketch, "E313", {"start": v(85.83, -10.56) * mm, "end": v(85.81, -10.55) * mm});
            skLineSegment(sketch, "E314", {"start": v(85.81, -10.55) * mm, "end": v(82.17, -8.59) * mm});
            skLineSegment(sketch, "E315", {"start": v(82.17, -8.59) * mm, "end": v(82.18, -8.59) * mm});
            skLineSegment(sketch, "E316", {"start": v(82.18, -8.59) * mm, "end": v(76.57, -6.16) * mm});
            skLineSegment(sketch, "E317", {"start": v(76.57, -6.16) * mm, "end": v(76.3, -5.91) * mm});
            skLineSegment(sketch, "E318", {"start": v(76.3, -5.91) * mm, "end": v(76.3, -5.9) * mm});
            skLineSegment(sketch, "E319", {"start": v(76.3, -5.9) * mm, "end": v(76.1, -5.31) * mm});
            skLineSegment(sketch, "E320", {"start": v(76.1, -5.31) * mm, "end": v(76.01, -4.7) * mm});
            skLineSegment(sketch, "E321", {"start": v(76.01, -4.7) * mm, "end": v(76.05, -4.3) * mm});
            skLineSegment(sketch, "E322", {"start": v(76.05, -4.3) * mm, "end": v(76.15, -3.92) * mm});
            skLineSegment(sketch, "E323", {"start": v(76.15, -3.92) * mm, "end": v(76.32, -3.57) * mm});
            skLineSegment(sketch, "E324", {"start": v(76.32, -3.57) * mm, "end": v(76.56, -3.25) * mm});
            skLineSegment(sketch, "E325", {"start": v(76.56, -3.25) * mm, "end": v(76.58, -3.21) * mm});
            skLineSegment(sketch, "E326", {"start": v(76.58, -3.21) * mm, "end": v(76.85, -2.98) * mm});
            skLineSegment(sketch, "E327", {"start": v(76.85, -2.98) * mm, "end": v(77.17, -2.81) * mm});
            skLineSegment(sketch, "E328", {"start": v(77.17, -2.81) * mm, "end": v(77.54, -2.71) * mm});
            skLineSegment(sketch, "E329", {"start": v(77.54, -2.71) * mm, "end": v(77.96, -2.68) * mm});
            skLineSegment(sketch, "E330", {"start": v(77.96, -2.68) * mm, "end": v(78.38, -2.71) * mm});
            skLineSegment(sketch, "E331", {"start": v(78.38, -2.71) * mm, "end": v(78.76, -2.82) * mm});
            skLineSegment(sketch, "E332", {"start": v(78.76, -2.82) * mm, "end": v(79.13, -3) * mm});
            skLineSegment(sketch, "E333", {"start": v(79.13, -3) * mm, "end": v(79.47, -3.24) * mm});
            skLineSegment(sketch, "E334", {"start": v(79.47, -3.24) * mm, "end": v(79.48, -3.24) * mm});
            skLineSegment(sketch, "E335", {"start": v(79.48, -3.24) * mm, "end": v(79.48, -3.25) * mm});
            skLineSegment(sketch, "E336", {"start": v(79.48, -3.25) * mm, "end": v(79.49, -3.25) * mm});
            skLineSegment(sketch, "E337", {"start": v(79.49, -3.25) * mm, "end": v(79.49, -3.26) * mm});
            skLineSegment(sketch, "E338", {"start": v(79.49, -3.26) * mm, "end": v(79.74, -3.56) * mm});
            skLineSegment(sketch, "E339", {"start": v(79.74, -3.56) * mm, "end": v(79.92, -3.92) * mm});
            skLineSegment(sketch, "E340", {"start": v(79.92, -3.92) * mm, "end": v(80.04, -4.34) * mm});
            skLineSegment(sketch, "E341", {"start": v(80.04, -4.34) * mm, "end": v(80.12, -5.1) * mm});
            skLineSegment(sketch, "E342", {"start": v(80.12, -5.1) * mm, "end": v(80.2, -5.36) * mm});
            skLineSegment(sketch, "E343", {"start": v(80.2, -5.36) * mm, "end": v(80.35, -5.6) * mm});
            skLineSegment(sketch, "E344", {"start": v(80.35, -5.6) * mm, "end": v(80.54, -5.83) * mm});
            skLineSegment(sketch, "E345", {"start": v(80.54, -5.83) * mm, "end": v(80.76, -6) * mm});
            skLineSegment(sketch, "E346", {"start": v(80.76, -6) * mm, "end": v(81, -6.13) * mm});
            skLineSegment(sketch, "E347", {"start": v(81, -6.13) * mm, "end": v(81.27, -6.2) * mm});
            skLineSegment(sketch, "E348", {"start": v(81.27, -6.2) * mm, "end": v(88.49, -6.2) * mm});
            skLineSegment(sketch, "E349", {"start": v(88.49, -6.2) * mm, "end": v(88.76, -6.13) * mm});
            skLineSegment(sketch, "E350", {"start": v(88.76, -6.13) * mm, "end": v(89, -6) * mm});
            skLineSegment(sketch, "E351", {"start": v(89, -6) * mm, "end": v(89.23, -5.81) * mm});
            skLineSegment(sketch, "E352", {"start": v(89.23, -5.81) * mm, "end": v(89.42, -5.58) * mm});
            skLineSegment(sketch, "E353", {"start": v(89.42, -5.58) * mm, "end": v(89.56, -5.33) * mm});
            skLineSegment(sketch, "E354", {"start": v(89.56, -5.33) * mm, "end": v(89.64, -5.06) * mm});
            skLineSegment(sketch, "E355", {"start": v(89.64, -5.06) * mm, "end": v(89.67, -4.76) * mm});
            skLineSegment(sketch, "E356", {"start": v(89.67, -4.76) * mm, "end": v(89.45, -2.42) * mm});
            skLineSegment(sketch, "E357", {"start": v(89.45, -2.42) * mm, "end": v(88.78, -0.22) * mm});
            skLineSegment(sketch, "E358", {"start": v(88.78, -0.22) * mm, "end": v(88.78, -0.21) * mm});
            skLineSegment(sketch, "E359", {"start": v(88.78, -0.21) * mm, "end": v(87.13, 2.7) * mm});
            skLineSegment(sketch, "E360", {"start": v(87.13, 2.7) * mm, "end": v(86.43, 3.52) * mm});
            skLineSegment(sketch, "E361", {"start": v(86.43, 3.52) * mm, "end": v(86.43, 3.52) * mm});
            skLineSegment(sketch, "E362", {"start": v(86.43, 3.52) * mm, "end": v(86.43, 3.53) * mm});
            skLineSegment(sketch, "E363", {"start": v(86.43, 3.53) * mm, "end": v(84.76, 4.91) * mm});
            skLineSegment(sketch, "E364", {"start": v(84.76, 4.91) * mm, "end": v(82.8, 5.96) * mm});
            skLineSegment(sketch, "E365", {"start": v(82.8, 5.96) * mm, "end": v(82.78, 5.97) * mm});
            skLineSegment(sketch, "E366", {"start": v(82.78, 5.97) * mm, "end": v(80.6, 6.67) * mm});
            skLineSegment(sketch, "E367", {"start": v(80.6, 6.67) * mm, "end": v(78.26, 6.9) * mm});
            skLineSegment(sketch, "E368", {"start": v(78.26, 6.9) * mm, "end": v(75.9, 6.68) * mm});
            skLineSegment(sketch, "E369", {"start": v(75.9, 6.68) * mm, "end": v(73.7, 6.01) * mm});
            skLineSegment(sketch, "E370", {"start": v(73.7, 6.01) * mm, "end": v(71.7, 4.97) * mm});
            skLineSegment(sketch, "E371", {"start": v(71.7, 4.97) * mm, "end": v(69.99, 3.63) * mm});
            skLineSegment(sketch, "E372", {"start": v(69.99, 3.63) * mm, "end": v(69.98, 3.63) * mm});
            skLineSegment(sketch, "E373", {"start": v(69.98, 3.63) * mm, "end": v(68.53, 1.93) * mm});
            skLineSegment(sketch, "E374", {"start": v(68.53, 1.93) * mm, "end": v(67.4, -0.11) * mm});
            skLineSegment(sketch, "E375", {"start": v(67.4, -0.11) * mm, "end": v(67.4, -0.1) * mm});
            skLineSegment(sketch, "E376", {"start": v(67.4, -0.1) * mm, "end": v(66.68, -2.35) * mm});
            skLineSegment(sketch, "E377", {"start": v(66.68, -2.35) * mm, "end": v(66.44, -4.76) * mm});
            skLineSegment(sketch, "E378", {"start": v(66.44, -4.76) * mm, "end": v(66.98, -8.49) * mm});
            skLineSegment(sketch, "E379", {"start": v(66.98, -8.49) * mm, "end": v(66.98, -8.5) * mm});
            skLineSegment(sketch, "E380", {"start": v(66.98, -8.5) * mm, "end": v(66.98, -8.5) * mm});
            skLineSegment(sketch, "E381", {"start": v(66.98, -8.5) * mm, "end": v(66.99, -8.5) * mm});
            skLineSegment(sketch, "E382", {"start": v(66.99, -8.5) * mm, "end": v(66.99, -8.52) * mm});
            skLineSegment(sketch, "E383", {"start": v(66.99, -8.52) * mm, "end": v(68.64, -11.64) * mm});
            skLineSegment(sketch, "E384", {"start": v(68.64, -11.64) * mm, "end": v(71.17, -14.07) * mm});
            skLineSegment(sketch, "E385", {"start": v(71.17, -14.07) * mm, "end": v(74.48, -15.8) * mm});
            skLineSegment(sketch, "E386", {"start": v(74.48, -15.8) * mm, "end": v(74.5, -15.8) * mm});
            skLineSegment(sketch, "E387", {"start": v(74.5, -15.8) * mm, "end": v(79.13, -17.64) * mm});
            skLineSegment(sketch, "E388", {"start": v(79.13, -17.64) * mm, "end": v(79.96, -18.3) * mm});
            skLineSegment(sketch, "E389", {"start": v(79.96, -18.3) * mm, "end": v(80.17, -18.67) * mm});
            skLineSegment(sketch, "E390", {"start": v(80.17, -18.67) * mm, "end": v(80.4, -19.48) * mm});
            skLineSegment(sketch, "E391", {"start": v(80.4, -19.48) * mm, "end": v(80.4, -20.44) * mm});
            skLineSegment(sketch, "E392", {"start": v(80.4, -20.44) * mm, "end": v(80.26, -20.88) * mm});
            skLineSegment(sketch, "E393", {"start": v(80.26, -20.88) * mm, "end": v(80.05, -21.27) * mm});
            skLineSegment(sketch, "E394", {"start": v(80.05, -21.27) * mm, "end": v(79.75, -21.6) * mm});
            skLineSegment(sketch, "E395", {"start": v(79.75, -21.6) * mm, "end": v(79.75, -21.6) * mm});
            skLineSegment(sketch, "E396", {"start": v(79.75, -21.6) * mm, "end": v(79.34, -21.89) * mm});
            skLineSegment(sketch, "E397", {"start": v(79.34, -21.89) * mm, "end": v(78.9, -22.09) * mm});
            skLineSegment(sketch, "E398", {"start": v(78.9, -22.09) * mm, "end": v(78.45, -22.21) * mm});
            skLineSegment(sketch, "E399", {"start": v(78.45, -22.21) * mm, "end": v(77.96, -22.26) * mm});
            skLineSegment(sketch, "E400", {"start": v(77.96, -22.26) * mm, "end": v(77.46, -22.22) * mm});
            skLineSegment(sketch, "E401", {"start": v(77.46, -22.22) * mm, "end": v(77.04, -22.11) * mm});
            skLineSegment(sketch, "E402", {"start": v(77.04, -22.11) * mm, "end": v(76.69, -21.93) * mm});
            skLineSegment(sketch, "E403", {"start": v(76.69, -21.93) * mm, "end": v(76.42, -21.68) * mm});
            skLineSegment(sketch, "E404", {"start": v(76.42, -21.68) * mm, "end": v(76.14, -21.2) * mm});
            skLineSegment(sketch, "E405", {"start": v(76.14, -21.2) * mm, "end": v(75.5, -19.1) * mm});
            skLineSegment(sketch, "E406", {"start": v(75.5, -19.1) * mm, "end": v(75.36, -18.88) * mm});
            skLineSegment(sketch, "E407", {"start": v(75.36, -18.88) * mm, "end": v(75.18, -18.68) * mm});
            skLineSegment(sketch, "E408", {"start": v(75.18, -18.68) * mm, "end": v(74.96, -18.52) * mm});
            skLineSegment(sketch, "E409", {"start": v(74.96, -18.52) * mm, "end": v(74.72, -18.41) * mm});
            skLineSegment(sketch, "E410", {"start": v(74.72, -18.41) * mm, "end": v(74.47, -18.34) * mm});
            skLineSegment(sketch, "E411", {"start": v(74.47, -18.34) * mm, "end": v(67.18, -18.37) * mm});
            skLineSegment(sketch, "E412", {"start": v(67.18, -18.37) * mm, "end": v(66.82, -18.53) * mm});
            skLineSegment(sketch, "E413", {"start": v(66.82, -18.53) * mm, "end": v(66.52, -18.78) * mm});
            skLineSegment(sketch, "E414", {"start": v(66.52, -18.78) * mm, "end": v(66.28, -19.1) * mm});
            skLineSegment(sketch, "E415", {"start": v(66.28, -19.1) * mm, "end": v(66.13, -19.45) * mm});
            skLineSegment(sketch, "E416", {"start": v(66.13, -19.45) * mm, "end": v(66.1, -19.83) * mm});
            skLineSegment(sketch, "E417", {"start": v(66.1, -19.83) * mm, "end": v(66.42, -22.62) * mm});
            skLineSegment(sketch, "E418", {"start": v(66.42, -22.62) * mm, "end": v(67.21, -25) * mm});
            skLineSegment(sketch, "E419", {"start": v(67.21, -25) * mm, "end": v(67.21, -24.97) * mm});
            skLineSegment(sketch, "E420", {"start": v(67.21, -24.97) * mm, "end": v(68.36, -27.05) * mm});
            skLineSegment(sketch, "E421", {"start": v(68.36, -27.05) * mm, "end": v(69.83, -28.72) * mm});
            skLineSegment(sketch, "E422", {"start": v(69.83, -28.72) * mm, "end": v(69.84, -28.73) * mm});
            skLineSegment(sketch, "E423", {"start": v(69.84, -28.73) * mm, "end": v(71.6, -30.06) * mm});
            skLineSegment(sketch, "E424", {"start": v(71.6, -30.06) * mm, "end": v(73.6, -31.04) * mm});
            skLineSegment(sketch, "E425", {"start": v(73.6, -31.04) * mm, "end": v(73.63, -31.04) * mm});
            skLineSegment(sketch, "E426", {"start": v(73.63, -31.04) * mm, "end": v(75.77, -31.61) * mm});
            skLineSegment(sketch, "E427", {"start": v(75.77, -31.61) * mm, "end": v(78.03, -31.8) * mm});
            skLineSegment(sketch, "E428", {"start": v(78.03, -31.8) * mm, "end": v(80.53, -31.58) * mm});
            skLineSegment(sketch, "E429", {"start": v(80.53, -31.58) * mm, "end": v(82.81, -30.89) * mm});
            skLineSegment(sketch, "E430", {"start": v(82.81, -30.89) * mm, "end": v(82.82, -30.88) * mm});
            skLineSegment(sketch, "E431", {"start": v(82.82, -30.88) * mm, "end": v(84.9, -29.74) * mm});
            skLineSegment(sketch, "E432", {"start": v(84.9, -29.74) * mm, "end": v(86.64, -28.26) * mm});
            skLineSegment(sketch, "E433", {"start": v(86.64, -28.26) * mm, "end": v(88.03, -26.5) * mm});
            skLineSegment(sketch, "E434", {"start": v(88.03, -26.5) * mm, "end": v(89.09, -24.47) * mm});
            skLineSegment(sketch, "E435", {"start": v(89.09, -24.47) * mm, "end": v(89.09, -24.48) * mm});
            skLineSegment(sketch, "E436", {"start": v(89.09, -24.48) * mm, "end": v(89.77, -22.22) * mm});
            skLineSegment(sketch, "E437", {"start": v(89.77, -22.22) * mm, "end": v(90, -19.8) * mm});
            skLineSegment(sketch, "E438", {"start": v(90, -19.8) * mm, "end": v(89.58, -16.45) * mm});
            skLineSegment(sketch, "E439", {"start": v(63.9, -2.74) * mm, "end": v(63.23, -0.26) * mm});
            skLineSegment(sketch, "E440", {"start": v(63.23, -0.26) * mm, "end": v(62.1, 1.94) * mm});
            skLineSegment(sketch, "E441", {"start": v(62.1, 1.94) * mm, "end": v(60.63, 3.72) * mm});
            skLineSegment(sketch, "E442", {"start": v(60.63, 3.72) * mm, "end": v(58.84, 5.12) * mm});
            skLineSegment(sketch, "E443", {"start": v(58.84, 5.12) * mm, "end": v(56.77, 6.11) * mm});
            skLineSegment(sketch, "E444", {"start": v(56.77, 6.11) * mm, "end": v(56.78, 6.11) * mm});
            skLineSegment(sketch, "E445", {"start": v(56.78, 6.11) * mm, "end": v(54.52, 6.7) * mm});
            skLineSegment(sketch, "E446", {"start": v(54.52, 6.7) * mm, "end": v(52.13, 6.9) * mm});
            skLineSegment(sketch, "E447", {"start": v(52.13, 6.9) * mm, "end": v(49.53, 6.67) * mm});
            skLineSegment(sketch, "E448", {"start": v(49.53, 6.67) * mm, "end": v(47.23, 5.97) * mm});
            skLineSegment(sketch, "E449", {"start": v(47.23, 5.97) * mm, "end": v(45.17, 4.91) * mm});
            skLineSegment(sketch, "E450", {"start": v(45.17, 4.91) * mm, "end": v(43.45, 3.5) * mm});
            skLineSegment(sketch, "E451", {"start": v(43.45, 3.5) * mm, "end": v(43.45, 3.5) * mm});
            skLineSegment(sketch, "E452", {"start": v(43.45, 3.5) * mm, "end": v(43.45, 3.49) * mm});
            skLineSegment(sketch, "E453", {"start": v(43.45, 3.49) * mm, "end": v(42.01, 1.75) * mm});
            skLineSegment(sketch, "E454", {"start": v(42.01, 1.75) * mm, "end": v(40.92, -0.29) * mm});
            skLineSegment(sketch, "E455", {"start": v(40.92, -0.29) * mm, "end": v(40.92, -0.3) * mm});
            skLineSegment(sketch, "E456", {"start": v(40.92, -0.3) * mm, "end": v(40.52, -1.38) * mm});
            skLineSegment(sketch, "E457", {"start": v(40.52, -1.38) * mm, "end": v(39.83, -5.24) * mm});
            skLineSegment(sketch, "E458", {"start": v(39.83, -5.24) * mm, "end": v(39.9, -5.63) * mm});
            skLineSegment(sketch, "E459", {"start": v(39.9, -5.63) * mm, "end": v(40.1, -6) * mm});
            skLineSegment(sketch, "E460", {"start": v(40.1, -6) * mm, "end": v(40.37, -6.28) * mm});
            skLineSegment(sketch, "E461", {"start": v(40.37, -6.28) * mm, "end": v(40.72, -6.5) * mm});
            skLineSegment(sketch, "E462", {"start": v(40.72, -6.5) * mm, "end": v(41.1, -6.6) * mm});
            skLineSegment(sketch, "E463", {"start": v(41.1, -6.6) * mm, "end": v(48.39, -6.6) * mm});
            skLineSegment(sketch, "E464", {"start": v(48.39, -6.6) * mm, "end": v(48.63, -6.53) * mm});
            skLineSegment(sketch, "E465", {"start": v(48.63, -6.53) * mm, "end": v(48.85, -6.42) * mm});
            skLineSegment(sketch, "E466", {"start": v(48.85, -6.42) * mm, "end": v(49.26, -6.1) * mm});
            skLineSegment(sketch, "E467", {"start": v(49.26, -6.1) * mm, "end": v(49.4, -5.9) * mm});
            skLineSegment(sketch, "E468", {"start": v(49.4, -5.9) * mm, "end": v(49.93, -4.41) * mm});
            skLineSegment(sketch, "E469", {"start": v(49.93, -4.41) * mm, "end": v(50.2, -4) * mm});
            skLineSegment(sketch, "E470", {"start": v(50.2, -4) * mm, "end": v(50.53, -3.67) * mm});
            skLineSegment(sketch, "E471", {"start": v(50.53, -3.67) * mm, "end": v(50.52, -3.67) * mm});
            skLineSegment(sketch, "E472", {"start": v(50.52, -3.67) * mm, "end": v(50.54, -3.66) * mm});
            skLineSegment(sketch, "E473", {"start": v(50.54, -3.66) * mm, "end": v(50.53, -3.67) * mm});
            skLineSegment(sketch, "E474", {"start": v(50.53, -3.67) * mm, "end": v(50.9, -3.42) * mm});
            skLineSegment(sketch, "E475", {"start": v(50.9, -3.42) * mm, "end": v(51.3, -3.24) * mm});
            skLineSegment(sketch, "E476", {"start": v(51.3, -3.24) * mm, "end": v(51.7, -3.13) * mm});
            skLineSegment(sketch, "E477", {"start": v(51.7, -3.13) * mm, "end": v(52.63, -3.12) * mm});
            skLineSegment(sketch, "E478", {"start": v(52.63, -3.12) * mm, "end": v(53.05, -3.22) * mm});
            skLineSegment(sketch, "E479", {"start": v(53.05, -3.22) * mm, "end": v(53.4, -3.38) * mm});
            skLineSegment(sketch, "E480", {"start": v(53.4, -3.38) * mm, "end": v(53.66, -3.6) * mm});
            skLineSegment(sketch, "E481", {"start": v(53.66, -3.6) * mm, "end": v(54.03, -4.57) * mm});
            skLineSegment(sketch, "E482", {"start": v(54.03, -4.57) * mm, "end": v(54.15, -7.85) * mm});
            skLineSegment(sketch, "E483", {"start": v(54.15, -7.85) * mm, "end": v(49, -7.93) * mm});
            skLineSegment(sketch, "E484", {"start": v(49, -7.93) * mm, "end": v(46.34, -8.52) * mm});
            skLineSegment(sketch, "E485", {"start": v(46.34, -8.52) * mm, "end": v(44.07, -9.63) * mm});
            skLineSegment(sketch, "E486", {"start": v(44.07, -9.63) * mm, "end": v(42.31, -11.17) * mm});
            skLineSegment(sketch, "E487", {"start": v(42.31, -11.17) * mm, "end": v(41.03, -13.12) * mm});
            skLineSegment(sketch, "E488", {"start": v(41.03, -13.12) * mm, "end": v(40.24, -15.53) * mm});
            skLineSegment(sketch, "E489", {"start": v(40.24, -15.53) * mm, "end": v(39.82, -18.1) * mm});
            skLineSegment(sketch, "E490", {"start": v(39.82, -18.1) * mm, "end": v(39.9, -24) * mm});
            skLineSegment(sketch, "E491", {"start": v(39.9, -24) * mm, "end": v(40.56, -26.32) * mm});
            skLineSegment(sketch, "E492", {"start": v(40.56, -26.32) * mm, "end": v(41.54, -28.24) * mm});
            skLineSegment(sketch, "E493", {"start": v(41.54, -28.24) * mm, "end": v(42.79, -29.68) * mm});
            skLineSegment(sketch, "E494", {"start": v(42.79, -29.68) * mm, "end": v(42.8, -29.68) * mm});
            skLineSegment(sketch, "E495", {"start": v(42.8, -29.68) * mm, "end": v(44.26, -30.74) * mm});
            skLineSegment(sketch, "E496", {"start": v(44.26, -30.74) * mm, "end": v(45.83, -31.39) * mm});
            skLineSegment(sketch, "E497", {"start": v(45.83, -31.39) * mm, "end": v(48.63, -31.8) * mm});
            skLineSegment(sketch, "E498", {"start": v(48.63, -31.8) * mm, "end": v(51.51, -31.48) * mm});
            skLineSegment(sketch, "E499", {"start": v(51.51, -31.48) * mm, "end": v(52.63, -31.08) * mm});
            skLineSegment(sketch, "E500", {"start": v(52.63, -31.08) * mm, "end": v(54.17, -30.05) * mm});
            skLineSegment(sketch, "E501", {"start": v(54.17, -30.05) * mm, "end": v(54.2, -30.3) * mm});
            skLineSegment(sketch, "E502", {"start": v(54.2, -30.3) * mm, "end": v(54.3, -30.55) * mm});
            skLineSegment(sketch, "E503", {"start": v(54.3, -30.55) * mm, "end": v(54.42, -30.77) * mm});
            skLineSegment(sketch, "E504", {"start": v(54.42, -30.77) * mm, "end": v(54.6, -30.97) * mm});
            skLineSegment(sketch, "E505", {"start": v(54.6, -30.97) * mm, "end": v(54.82, -31.16) * mm});
            skLineSegment(sketch, "E506", {"start": v(54.82, -31.16) * mm, "end": v(55.07, -31.3) * mm});
            skLineSegment(sketch, "E507", {"start": v(55.07, -31.3) * mm, "end": v(55.34, -31.37) * mm});
            skLineSegment(sketch, "E508", {"start": v(55.34, -31.37) * mm, "end": v(62.95, -31.37) * mm});
            skLineSegment(sketch, "E509", {"start": v(62.95, -31.37) * mm, "end": v(63.22, -31.3) * mm});
            skLineSegment(sketch, "E510", {"start": v(63.22, -31.3) * mm, "end": v(63.47, -31.16) * mm});
            skLineSegment(sketch, "E511", {"start": v(63.47, -31.16) * mm, "end": v(63.7, -30.97) * mm});
            skLineSegment(sketch, "E512", {"start": v(63.7, -30.97) * mm, "end": v(63.9, -30.74) * mm});
            skLineSegment(sketch, "E513", {"start": v(63.9, -30.74) * mm, "end": v(64.03, -30.5) * mm});
            skLineSegment(sketch, "E514", {"start": v(64.03, -30.5) * mm, "end": v(64.11, -30.22) * mm});
            skLineSegment(sketch, "E515", {"start": v(64.11, -30.22) * mm, "end": v(63.9, -2.74) * mm});
            skLineSegment(sketch, "E516", {"start": v(37.42, -18.99) * mm, "end": v(37.23, -18.76) * mm});
            skLineSegment(sketch, "E517", {"start": v(37.23, -18.76) * mm, "end": v(37, -18.57) * mm});
            skLineSegment(sketch, "E518", {"start": v(37, -18.57) * mm, "end": v(36.75, -18.43) * mm});
            skLineSegment(sketch, "E519", {"start": v(36.75, -18.43) * mm, "end": v(36.48, -18.35) * mm});
            skLineSegment(sketch, "E520", {"start": v(36.48, -18.35) * mm, "end": v(28.9, -18.34) * mm});
            skLineSegment(sketch, "E521", {"start": v(28.9, -18.34) * mm, "end": v(28.64, -18.41) * mm});
            skLineSegment(sketch, "E522", {"start": v(28.64, -18.41) * mm, "end": v(28.4, -18.53) * mm});
            skLineSegment(sketch, "E523", {"start": v(28.4, -18.53) * mm, "end": v(28, -18.9) * mm});
            skLineSegment(sketch, "E524", {"start": v(28, -18.9) * mm, "end": v(27.86, -19.12) * mm});
            skLineSegment(sketch, "E525", {"start": v(27.86, -19.12) * mm, "end": v(27.76, -19.37) * mm});
            skLineSegment(sketch, "E526", {"start": v(27.76, -19.37) * mm, "end": v(27.5, -20.52) * mm});
            skLineSegment(sketch, "E527", {"start": v(27.5, -20.52) * mm, "end": v(27.12, -21.41) * mm});
            skLineSegment(sketch, "E528", {"start": v(27.12, -21.41) * mm, "end": v(26.88, -21.6) * mm});
            skLineSegment(sketch, "E529", {"start": v(26.88, -21.6) * mm, "end": v(26.57, -21.73) * mm});
            skLineSegment(sketch, "E530", {"start": v(26.57, -21.73) * mm, "end": v(25.73, -21.83) * mm});
            skLineSegment(sketch, "E531", {"start": v(25.73, -21.83) * mm, "end": v(24.9, -21.71) * mm});
            skLineSegment(sketch, "E532", {"start": v(24.9, -21.71) * mm, "end": v(24.54, -21.57) * mm});
            skLineSegment(sketch, "E533", {"start": v(24.54, -21.57) * mm, "end": v(24.24, -21.36) * mm});
            skLineSegment(sketch, "E534", {"start": v(24.24, -21.36) * mm, "end": v(24.02, -21.07) * mm});
            skLineSegment(sketch, "E535", {"start": v(24.02, -21.07) * mm, "end": v(23.87, -20.72) * mm});
            skLineSegment(sketch, "E536", {"start": v(23.87, -20.72) * mm, "end": v(23.78, -20.32) * mm});
            skLineSegment(sketch, "E537", {"start": v(23.78, -20.32) * mm, "end": v(23.75, -16.6) * mm});
            skLineSegment(sketch, "E538", {"start": v(23.75, -16.6) * mm, "end": v(36.48, -16.57) * mm});
            skLineSegment(sketch, "E539", {"start": v(36.48, -16.57) * mm, "end": v(36.75, -16.5) * mm});
            skLineSegment(sketch, "E540", {"start": v(36.75, -16.5) * mm, "end": v(37, -16.36) * mm});
            skLineSegment(sketch, "E541", {"start": v(37, -16.36) * mm, "end": v(37.23, -16.17) * mm});
            skLineSegment(sketch, "E542", {"start": v(37.23, -16.17) * mm, "end": v(37.42, -15.94) * mm});
            skLineSegment(sketch, "E543", {"start": v(37.42, -15.94) * mm, "end": v(37.56, -15.69) * mm});
            skLineSegment(sketch, "E544", {"start": v(37.56, -15.69) * mm, "end": v(37.64, -15.42) * mm});
            skLineSegment(sketch, "E545", {"start": v(37.64, -15.42) * mm, "end": v(37.47, -3.02) * mm});
            skLineSegment(sketch, "E546", {"start": v(37.47, -3.02) * mm, "end": v(36.89, -0.72) * mm});
            skLineSegment(sketch, "E547", {"start": v(36.89, -0.72) * mm, "end": v(36.88, -0.7) * mm});
            skLineSegment(sketch, "E548", {"start": v(36.88, -0.7) * mm, "end": v(36.87, -0.68) * mm});
            skLineSegment(sketch, "E549", {"start": v(36.87, -0.68) * mm, "end": v(35.85, 1.43) * mm});
            skLineSegment(sketch, "E550", {"start": v(35.85, 1.43) * mm, "end": v(34.5, 3.25) * mm});
            skLineSegment(sketch, "E551", {"start": v(34.5, 3.25) * mm, "end": v(32.77, 4.78) * mm});
            skLineSegment(sketch, "E552", {"start": v(32.77, 4.78) * mm, "end": v(30.7, 5.93) * mm});
            skLineSegment(sketch, "E553", {"start": v(30.7, 5.93) * mm, "end": v(30.7, 5.94) * mm});
            skLineSegment(sketch, "E554", {"start": v(30.7, 5.94) * mm, "end": v(28.35, 6.66) * mm});
            skLineSegment(sketch, "E555", {"start": v(28.35, 6.66) * mm, "end": v(25.73, 6.9) * mm});
            skLineSegment(sketch, "E556", {"start": v(25.73, 6.9) * mm, "end": v(22.32, 6.5) * mm});
            skLineSegment(sketch, "E557", {"start": v(22.32, 6.5) * mm, "end": v(19.4, 5.31) * mm});
            skLineSegment(sketch, "E558", {"start": v(19.4, 5.31) * mm, "end": v(17.01, 3.46) * mm});
            skLineSegment(sketch, "E559", {"start": v(17.01, 3.46) * mm, "end": v(15.25, 1.07) * mm});
            skLineSegment(sketch, "E560", {"start": v(15.25, 1.07) * mm, "end": v(14.54, -0.64) * mm});
            skLineSegment(sketch, "E561", {"start": v(14.54, -0.64) * mm, "end": v(13.8, -6.67) * mm});
            skLineSegment(sketch, "E562", {"start": v(13.8, -6.67) * mm, "end": v(14.54, -24.32) * mm});
            skLineSegment(sketch, "E563", {"start": v(14.54, -24.32) * mm, "end": v(15.25, -26.02) * mm});
            skLineSegment(sketch, "E564", {"start": v(15.25, -26.02) * mm, "end": v(17.01, -28.39) * mm});
            skLineSegment(sketch, "E565", {"start": v(17.01, -28.39) * mm, "end": v(19.4, -30.23) * mm});
            skLineSegment(sketch, "E566", {"start": v(19.4, -30.23) * mm, "end": v(22.32, -31.41) * mm});
            skLineSegment(sketch, "E567", {"start": v(22.32, -31.41) * mm, "end": v(25.73, -31.8) * mm});
            skLineSegment(sketch, "E568", {"start": v(25.73, -31.8) * mm, "end": v(28.34, -31.57) * mm});
            skLineSegment(sketch, "E569", {"start": v(28.34, -31.57) * mm, "end": v(30.65, -30.88) * mm});
            skLineSegment(sketch, "E570", {"start": v(30.65, -30.88) * mm, "end": v(30.66, -30.88) * mm});
            skLineSegment(sketch, "E571", {"start": v(30.66, -30.88) * mm, "end": v(32.7, -29.76) * mm});
            skLineSegment(sketch, "E572", {"start": v(32.7, -29.76) * mm, "end": v(34.43, -28.28) * mm});
            skLineSegment(sketch, "E573", {"start": v(34.43, -28.28) * mm, "end": v(35.83, -26.52) * mm});
            skLineSegment(sketch, "E574", {"start": v(35.83, -26.52) * mm, "end": v(36.86, -24.49) * mm});
            skLineSegment(sketch, "E575", {"start": v(36.86, -24.49) * mm, "end": v(36.86, -24.48) * mm});
            skLineSegment(sketch, "E576", {"start": v(36.86, -24.48) * mm, "end": v(36.87, -24.47) * mm});
            skLineSegment(sketch, "E577", {"start": v(36.87, -24.47) * mm, "end": v(36.87, -24.45) * mm});
            skLineSegment(sketch, "E578", {"start": v(36.87, -24.45) * mm, "end": v(37.22, -23.36) * mm});
            skLineSegment(sketch, "E579", {"start": v(37.22, -23.36) * mm, "end": v(37.64, -19.5) * mm});
            skLineSegment(sketch, "E580", {"start": v(37.64, -19.5) * mm, "end": v(37.56, -19.24) * mm});
            skLineSegment(sketch, "E581", {"start": v(37.56, -19.24) * mm, "end": v(37.42, -18.99) * mm});
            skLineSegment(sketch, "E582", {"start": v(27.56, -4.46) * mm, "end": v(27.4, -4) * mm});
            skLineSegment(sketch, "E583", {"start": v(27.4, -4) * mm, "end": v(27.17, -3.62) * mm});
            skLineSegment(sketch, "E584", {"start": v(27.17, -3.62) * mm, "end": v(26.87, -3.39) * mm});
            skLineSegment(sketch, "E585", {"start": v(26.87, -3.39) * mm, "end": v(26.53, -3.22) * mm});
            skLineSegment(sketch, "E586", {"start": v(26.53, -3.22) * mm, "end": v(26.15, -3.12) * mm});
            skLineSegment(sketch, "E587", {"start": v(26.15, -3.12) * mm, "end": v(25.73, -3.09) * mm});
            skLineSegment(sketch, "E588", {"start": v(25.73, -3.09) * mm, "end": v(25.3, -3.12) * mm});
            skLineSegment(sketch, "E589", {"start": v(25.3, -3.12) * mm, "end": v(24.92, -3.22) * mm});
            skLineSegment(sketch, "E590", {"start": v(24.92, -3.22) * mm, "end": v(24.58, -3.4) * mm});
            skLineSegment(sketch, "E591", {"start": v(24.58, -3.4) * mm, "end": v(24.29, -3.63) * mm});
            skLineSegment(sketch, "E592", {"start": v(24.29, -3.63) * mm, "end": v(24.28, -3.63) * mm});
            skLineSegment(sketch, "E593", {"start": v(24.28, -3.63) * mm, "end": v(24.05, -4.01) * mm});
            skLineSegment(sketch, "E594", {"start": v(24.05, -4.01) * mm, "end": v(23.88, -4.47) * mm});
            skLineSegment(sketch, "E595", {"start": v(23.88, -4.47) * mm, "end": v(23.75, -8.13) * mm});
            skLineSegment(sketch, "E596", {"start": v(23.75, -8.13) * mm, "end": v(27.7, -8.13) * mm});
            skLineSegment(sketch, "E597", {"start": v(27.7, -8.13) * mm, "end": v(27.56, -4.46) * mm});
            skLineSegment(sketch, "E598", {"start": v(53.6, -16.17) * mm, "end": v(52, -16.39) * mm});
            skLineSegment(sketch, "E599", {"start": v(52, -16.39) * mm, "end": v(50.64, -17) * mm});
            skLineSegment(sketch, "E600", {"start": v(50.64, -17) * mm, "end": v(50.22, -17.45) * mm});
            skLineSegment(sketch, "E601", {"start": v(50.22, -17.45) * mm, "end": v(49.92, -18.05) * mm});
            skLineSegment(sketch, "E602", {"start": v(49.92, -18.05) * mm, "end": v(49.74, -18.79) * mm});
            skLineSegment(sketch, "E603", {"start": v(49.74, -18.79) * mm, "end": v(49.68, -19.67) * mm});
            skLineSegment(sketch, "E604", {"start": v(49.68, -19.67) * mm, "end": v(49.85, -20.96) * mm});
            skLineSegment(sketch, "E605", {"start": v(49.85, -20.96) * mm, "end": v(50.06, -21.5) * mm});
            skLineSegment(sketch, "E606", {"start": v(50.06, -21.5) * mm, "end": v(50.35, -22) * mm});
            skLineSegment(sketch, "E607", {"start": v(50.35, -22) * mm, "end": v(50.36, -22.02) * mm});
            skLineSegment(sketch, "E608", {"start": v(50.36, -22.02) * mm, "end": v(50.65, -22.3) * mm});
            skLineSegment(sketch, "E609", {"start": v(50.65, -22.3) * mm, "end": v(51, -22.5) * mm});
            skLineSegment(sketch, "E610", {"start": v(51, -22.5) * mm, "end": v(51.4, -22.62) * mm});
            skLineSegment(sketch, "E611", {"start": v(51.4, -22.62) * mm, "end": v(51.87, -22.66) * mm});
            skLineSegment(sketch, "E612", {"start": v(51.87, -22.66) * mm, "end": v(52.36, -22.62) * mm});
            skLineSegment(sketch, "E613", {"start": v(52.36, -22.62) * mm, "end": v(52.8, -22.5) * mm});
            skLineSegment(sketch, "E614", {"start": v(52.8, -22.5) * mm, "end": v(53.19, -22.3) * mm});
            skLineSegment(sketch, "E615", {"start": v(53.19, -22.3) * mm, "end": v(53.53, -22.02) * mm});
            skLineSegment(sketch, "E616", {"start": v(53.53, -22.02) * mm, "end": v(53.8, -21.55) * mm});
            skLineSegment(sketch, "E617", {"start": v(53.8, -21.55) * mm, "end": v(54, -21) * mm});
            skLineSegment(sketch, "E618", {"start": v(54, -21) * mm, "end": v(54.15, -16.23) * mm});
            skLineSegment(sketch, "E619", {"start": v(54.15, -16.23) * mm, "end": v(53.6, -16.17) * mm});
            skLineSegment(sketch, "E620", {"start": v(11.32, 19.4) * mm, "end": v(11.24, 19.67) * mm});
            skLineSegment(sketch, "E621", {"start": v(11.24, 19.67) * mm, "end": v(11.1, 19.92) * mm});
            skLineSegment(sketch, "E622", {"start": v(11.1, 19.92) * mm, "end": v(10.91, 20.15) * mm});
            skLineSegment(sketch, "E623", {"start": v(10.91, 20.15) * mm, "end": v(10.69, 20.34) * mm});
            skLineSegment(sketch, "E624", {"start": v(10.69, 20.34) * mm, "end": v(10.44, 20.47) * mm});
            skLineSegment(sketch, "E625", {"start": v(10.44, 20.47) * mm, "end": v(10.17, 20.55) * mm});
            skLineSegment(sketch, "E626", {"start": v(10.17, 20.55) * mm, "end": v(2.55, 20.55) * mm});
            skLineSegment(sketch, "E627", {"start": v(2.55, 20.55) * mm, "end": v(2.28, 20.47) * mm});
            skLineSegment(sketch, "E628", {"start": v(2.28, 20.47) * mm, "end": v(2.03, 20.34) * mm});
            skLineSegment(sketch, "E629", {"start": v(2.03, 20.34) * mm, "end": v(1.8, 20.15) * mm});
            skLineSegment(sketch, "E630", {"start": v(1.8, 20.15) * mm, "end": v(1.61, 19.92) * mm});
            skLineSegment(sketch, "E631", {"start": v(1.61, 19.92) * mm, "end": v(1.48, 19.67) * mm});
            skLineSegment(sketch, "E632", {"start": v(1.48, 19.67) * mm, "end": v(1.4, 19.4) * mm});
            skLineSegment(sketch, "E633", {"start": v(1.4, 19.4) * mm, "end": v(1.37, 5.3) * mm});
            skLineSegment(sketch, "E634", {"start": v(1.37, 5.3) * mm, "end": v(0.66, 5.75) * mm});
            skLineSegment(sketch, "E635", {"start": v(0.66, 5.75) * mm, "end": v(0.66, 5.76) * mm});
            skLineSegment(sketch, "E636", {"start": v(0.66, 5.76) * mm, "end": v(-0.35, 6.26) * mm});
            skLineSegment(sketch, "E637", {"start": v(-0.35, 6.26) * mm, "end": v(-2.57, 6.83) * mm});
            skLineSegment(sketch, "E638", {"start": v(-2.57, 6.83) * mm, "end": v(-5.24, 6.83) * mm});
            skLineSegment(sketch, "E639", {"start": v(-5.24, 6.83) * mm, "end": v(-7.62, 6.25) * mm});
            skLineSegment(sketch, "E640", {"start": v(-7.62, 6.25) * mm, "end": v(-8.55, 5.75) * mm});
            skLineSegment(sketch, "E641", {"start": v(-8.55, 5.75) * mm, "end": v(-10.06, 4.54) * mm});
            skLineSegment(sketch, "E642", {"start": v(-10.06, 4.54) * mm, "end": v(-11.27, 3.04) * mm});
            skLineSegment(sketch, "E643", {"start": v(-11.27, 3.04) * mm, "end": v(-11.27, 3.03) * mm});
            skLineSegment(sketch, "E644", {"start": v(-11.27, 3.03) * mm, "end": v(-11.27, 3.02) * mm});
            skLineSegment(sketch, "E645", {"start": v(-11.27, 3.02) * mm, "end": v(-12, 1.48) * mm});
            skLineSegment(sketch, "E646", {"start": v(-12, 1.48) * mm, "end": v(-12.42, -0.55) * mm});
            skLineSegment(sketch, "E647", {"start": v(-12.42, -0.55) * mm, "end": v(-12.34, -24.3) * mm});
            skLineSegment(sketch, "E648", {"start": v(-12.34, -24.3) * mm, "end": v(-11.9, -26.21) * mm});
            skLineSegment(sketch, "E649", {"start": v(-11.9, -26.21) * mm, "end": v(-11.27, -27.74) * mm});
            skLineSegment(sketch, "E650", {"start": v(-11.27, -27.74) * mm, "end": v(-10, -29.52) * mm});
            skLineSegment(sketch, "E651", {"start": v(-10, -29.52) * mm, "end": v(-8.34, -30.8) * mm});
            skLineSegment(sketch, "E652", {"start": v(-8.34, -30.8) * mm, "end": v(-6.3, -31.55) * mm});
            skLineSegment(sketch, "E653", {"start": v(-6.3, -31.55) * mm, "end": v(-3.84, -31.8) * mm});
            skLineSegment(sketch, "E654", {"start": v(-3.84, -31.8) * mm, "end": v(-1.38, -31.53) * mm});
            skLineSegment(sketch, "E655", {"start": v(-1.38, -31.53) * mm, "end": v(0.74, -30.68) * mm});
            skLineSegment(sketch, "E656", {"start": v(0.74, -30.68) * mm, "end": v(1.4, -30.2) * mm});
            skLineSegment(sketch, "E657", {"start": v(1.4, -30.2) * mm, "end": v(1.45, -30.42) * mm});
            skLineSegment(sketch, "E658", {"start": v(1.45, -30.42) * mm, "end": v(1.53, -30.61) * mm});
            skLineSegment(sketch, "E659", {"start": v(1.53, -30.61) * mm, "end": v(1.8, -30.97) * mm});
            skLineSegment(sketch, "E660", {"start": v(1.8, -30.97) * mm, "end": v(2.03, -31.16) * mm});
            skLineSegment(sketch, "E661", {"start": v(2.03, -31.16) * mm, "end": v(2.28, -31.3) * mm});
            skLineSegment(sketch, "E662", {"start": v(2.28, -31.3) * mm, "end": v(2.55, -31.37) * mm});
            skLineSegment(sketch, "E663", {"start": v(2.55, -31.37) * mm, "end": v(10.17, -31.37) * mm});
            skLineSegment(sketch, "E664", {"start": v(10.17, -31.37) * mm, "end": v(10.44, -31.3) * mm});
            skLineSegment(sketch, "E665", {"start": v(10.44, -31.3) * mm, "end": v(10.69, -31.16) * mm});
            skLineSegment(sketch, "E666", {"start": v(10.69, -31.16) * mm, "end": v(10.91, -30.97) * mm});
            skLineSegment(sketch, "E667", {"start": v(10.91, -30.97) * mm, "end": v(11.1, -30.74) * mm});
            skLineSegment(sketch, "E668", {"start": v(11.1, -30.74) * mm, "end": v(11.24, -30.5) * mm});
            skLineSegment(sketch, "E669", {"start": v(11.24, -30.5) * mm, "end": v(11.32, -30.22) * mm});
            skLineSegment(sketch, "E670", {"start": v(11.32, -30.22) * mm, "end": v(11.35, 19.1) * mm});
            skLineSegment(sketch, "E671", {"start": v(11.35, 19.1) * mm, "end": v(11.32, 19.4) * mm});
            skLineSegment(sketch, "E672", {"start": v(1.22, -4.46) * mm, "end": v(1.03, -4.05) * mm});
            skLineSegment(sketch, "E673", {"start": v(1.03, -4.05) * mm, "end": v(0.76, -3.69) * mm});
            skLineSegment(sketch, "E674", {"start": v(0.76, -3.69) * mm, "end": v(0.45, -3.42) * mm});
            skLineSegment(sketch, "E675", {"start": v(0.45, -3.42) * mm, "end": v(0.11, -3.23) * mm});
            skLineSegment(sketch, "E676", {"start": v(0.11, -3.23) * mm, "end": v(-0.27, -3.12) * mm});
            skLineSegment(sketch, "E677", {"start": v(-0.27, -3.12) * mm, "end": v(-1.15, -3.12) * mm});
            skLineSegment(sketch, "E678", {"start": v(-1.15, -3.12) * mm, "end": v(-1.56, -3.22) * mm});
            skLineSegment(sketch, "E679", {"start": v(-1.56, -3.22) * mm, "end": v(-1.89, -3.39) * mm});
            skLineSegment(sketch, "E680", {"start": v(-1.89, -3.39) * mm, "end": v(-2.14, -3.62) * mm});
            skLineSegment(sketch, "E681", {"start": v(-2.14, -3.62) * mm, "end": v(-2.52, -4.6) * mm});
            skLineSegment(sketch, "E682", {"start": v(-2.52, -4.6) * mm, "end": v(-2.64, -5.74) * mm});
            skLineSegment(sketch, "E683", {"start": v(-2.64, -5.74) * mm, "end": v(-2.5, -20.04) * mm});
            skLineSegment(sketch, "E684", {"start": v(-2.5, -20.04) * mm, "end": v(-2.06, -21.2) * mm});
            skLineSegment(sketch, "E685", {"start": v(-2.06, -21.2) * mm, "end": v(-2.07, -21.19) * mm});
            skLineSegment(sketch, "E686", {"start": v(-2.07, -21.19) * mm, "end": v(-1.81, -21.47) * mm});
            skLineSegment(sketch, "E687", {"start": v(-1.81, -21.47) * mm, "end": v(-1.5, -21.67) * mm});
            skLineSegment(sketch, "E688", {"start": v(-1.5, -21.67) * mm, "end": v(-1.11, -21.79) * mm});
            skLineSegment(sketch, "E689", {"start": v(-1.11, -21.79) * mm, "end": v(-0.68, -21.83) * mm});
            skLineSegment(sketch, "E690", {"start": v(-0.68, -21.83) * mm, "end": v(-0.26, -21.8) * mm});
            skLineSegment(sketch, "E691", {"start": v(-0.26, -21.8) * mm, "end": v(0.12, -21.67) * mm});
            skLineSegment(sketch, "E692", {"start": v(0.12, -21.67) * mm, "end": v(0.45, -21.47) * mm});
            skLineSegment(sketch, "E693", {"start": v(0.45, -21.47) * mm, "end": v(0.74, -21.19) * mm});
            skLineSegment(sketch, "E694", {"start": v(0.74, -21.19) * mm, "end": v(0.72, -21.2) * mm});
            skLineSegment(sketch, "E695", {"start": v(0.72, -21.2) * mm, "end": v(1, -20.74) * mm});
            skLineSegment(sketch, "E696", {"start": v(1, -20.74) * mm, "end": v(1.2, -20.21) * mm});
            skLineSegment(sketch, "E697", {"start": v(1.2, -20.21) * mm, "end": v(1.33, -4.9) * mm});
            skLineSegment(sketch, "E698", {"start": v(1.33, -4.9) * mm, "end": v(1.22, -4.46) * mm});
            skLineSegment(sketch, "E699", {"start": v(-40.34, 19.4) * mm, "end": v(-40.43, 19.67) * mm});
            skLineSegment(sketch, "E700", {"start": v(-40.43, 19.67) * mm, "end": v(-40.56, 19.92) * mm});
            skLineSegment(sketch, "E701", {"start": v(-40.56, 19.92) * mm, "end": v(-40.76, 20.15) * mm});
            skLineSegment(sketch, "E702", {"start": v(-40.76, 20.15) * mm, "end": v(-40.98, 20.34) * mm});
            skLineSegment(sketch, "E703", {"start": v(-40.98, 20.34) * mm, "end": v(-41.23, 20.47) * mm});
            skLineSegment(sketch, "E704", {"start": v(-41.23, 20.47) * mm, "end": v(-41.5, 20.55) * mm});
            skLineSegment(sketch, "E705", {"start": v(-41.5, 20.55) * mm, "end": v(-65.37, 20.55) * mm});
            skLineSegment(sketch, "E706", {"start": v(-65.37, 20.55) * mm, "end": v(-65.65, 20.47) * mm});
            skLineSegment(sketch, "E707", {"start": v(-65.65, 20.47) * mm, "end": v(-65.9, 20.34) * mm});
            skLineSegment(sketch, "E708", {"start": v(-65.9, 20.34) * mm, "end": v(-66.12, 20.15) * mm});
            skLineSegment(sketch, "E709", {"start": v(-66.12, 20.15) * mm, "end": v(-66.31, 19.92) * mm});
            skLineSegment(sketch, "E710", {"start": v(-66.31, 19.92) * mm, "end": v(-66.45, 19.67) * mm});
            skLineSegment(sketch, "E711", {"start": v(-66.45, 19.67) * mm, "end": v(-66.53, 19.4) * mm});
            skLineSegment(sketch, "E712", {"start": v(-66.53, 19.4) * mm, "end": v(-66.56, 18.85) * mm});
            skLineSegment(sketch, "E713", {"start": v(-66.56, 18.85) * mm, "end": v(-65.19, 17.64) * mm});
            skLineSegment(sketch, "E714", {"start": v(-65.19, 17.64) * mm, "end": v(-64.01, 16.2) * mm});
            skLineSegment(sketch, "E715", {"start": v(-64.01, 16.2) * mm, "end": v(-62.26, 12.65) * mm});
            skLineSegment(sketch, "E716", {"start": v(-62.26, 12.65) * mm, "end": v(-61.8, 11.03) * mm});
            skLineSegment(sketch, "E717", {"start": v(-61.8, 11.03) * mm, "end": v(-58.4, 11.03) * mm});
            skLineSegment(sketch, "E718", {"start": v(-58.4, 11.03) * mm, "end": v(-58.37, -30.22) * mm});
            skLineSegment(sketch, "E719", {"start": v(-58.37, -30.22) * mm, "end": v(-58.3, -30.5) * mm});
            skLineSegment(sketch, "E720", {"start": v(-58.3, -30.5) * mm, "end": v(-58.16, -30.74) * mm});
            skLineSegment(sketch, "E721", {"start": v(-58.16, -30.74) * mm, "end": v(-57.97, -30.97) * mm});
            skLineSegment(sketch, "E722", {"start": v(-57.97, -30.97) * mm, "end": v(-57.74, -31.16) * mm});
            skLineSegment(sketch, "E723", {"start": v(-57.74, -31.16) * mm, "end": v(-57.5, -31.3) * mm});
            skLineSegment(sketch, "E724", {"start": v(-57.5, -31.3) * mm, "end": v(-57.22, -31.37) * mm});
            skLineSegment(sketch, "E725", {"start": v(-57.22, -31.37) * mm, "end": v(-49.64, -31.37) * mm});
            skLineSegment(sketch, "E726", {"start": v(-49.64, -31.37) * mm, "end": v(-49.37, -31.3) * mm});
            skLineSegment(sketch, "E727", {"start": v(-49.37, -31.3) * mm, "end": v(-49.12, -31.16) * mm});
            skLineSegment(sketch, "E728", {"start": v(-49.12, -31.16) * mm, "end": v(-48.89, -30.97) * mm});
            skLineSegment(sketch, "E729", {"start": v(-48.89, -30.97) * mm, "end": v(-48.7, -30.74) * mm});
            skLineSegment(sketch, "E730", {"start": v(-48.7, -30.74) * mm, "end": v(-48.57, -30.5) * mm});
            skLineSegment(sketch, "E731", {"start": v(-48.57, -30.5) * mm, "end": v(-48.49, -30.22) * mm});
            skLineSegment(sketch, "E732", {"start": v(-48.49, -30.22) * mm, "end": v(-48.46, 11.03) * mm});
            skLineSegment(sketch, "E733", {"start": v(-48.46, 11.03) * mm, "end": v(-41.5, 11.06) * mm});
            skLineSegment(sketch, "E734", {"start": v(-41.5, 11.06) * mm, "end": v(-41.23, 11.14) * mm});
            skLineSegment(sketch, "E735", {"start": v(-41.23, 11.14) * mm, "end": v(-40.98, 11.28) * mm});
            skLineSegment(sketch, "E736", {"start": v(-40.98, 11.28) * mm, "end": v(-40.76, 11.47) * mm});
            skLineSegment(sketch, "E737", {"start": v(-40.76, 11.47) * mm, "end": v(-40.56, 11.7) * mm});
            skLineSegment(sketch, "E738", {"start": v(-40.56, 11.7) * mm, "end": v(-40.43, 11.95) * mm});
            skLineSegment(sketch, "E739", {"start": v(-40.43, 11.95) * mm, "end": v(-40.34, 12.22) * mm});
            skLineSegment(sketch, "E740", {"start": v(-40.34, 12.22) * mm, "end": v(-40.32, 19.1) * mm});
            skLineSegment(sketch, "E741", {"start": v(-40.32, 19.1) * mm, "end": v(-40.34, 19.4) * mm});
            skLineSegment(sketch, "E742", {"start": v(-61.88, -29.68) * mm, "end": v(-69.12, -8.19) * mm});
            skLineSegment(sketch, "E743", {"start": v(-69.12, -8.19) * mm, "end": v(-66.96, -6.4) * mm});
            skLineSegment(sketch, "E744", {"start": v(-66.96, -6.4) * mm, "end": v(-66.97, -6.4) * mm});
            skLineSegment(sketch, "E745", {"start": v(-66.97, -6.4) * mm, "end": v(-65.75, -4.9) * mm});
            skLineSegment(sketch, "E746", {"start": v(-65.75, -4.9) * mm, "end": v(-64.82, -3.21) * mm});
            skLineSegment(sketch, "E747", {"start": v(-64.82, -3.21) * mm, "end": v(-64.82, -3.22) * mm});
            skLineSegment(sketch, "E748", {"start": v(-64.82, -3.22) * mm, "end": v(-63.73, 0.42) * mm});
            skLineSegment(sketch, "E749", {"start": v(-63.73, 0.42) * mm, "end": v(-63.36, 4.72) * mm});
            skLineSegment(sketch, "E750", {"start": v(-63.36, 4.72) * mm, "end": v(-64.25, 11.77) * mm});
            skLineSegment(sketch, "E751", {"start": v(-64.25, 11.77) * mm, "end": v(-64.26, 11.78) * mm});
            skLineSegment(sketch, "E752", {"start": v(-64.26, 11.78) * mm, "end": v(-64.26, 11.78) * mm});
            skLineSegment(sketch, "E753", {"start": v(-64.26, 11.78) * mm, "end": v(-64.43, 12.35) * mm});
            skLineSegment(sketch, "E754", {"start": v(-64.43, 12.35) * mm, "end": v(-64.43, 12.37) * mm});
            skLineSegment(sketch, "E755", {"start": v(-64.43, 12.37) * mm, "end": v(-66.28, 15.98) * mm});
            skLineSegment(sketch, "E756", {"start": v(-66.28, 15.98) * mm, "end": v(-69.03, 18.56) * mm});
            skLineSegment(sketch, "E757", {"start": v(-69.03, 18.56) * mm, "end": v(-72.7, 20.1) * mm});
            skLineSegment(sketch, "E758", {"start": v(-72.7, 20.1) * mm, "end": v(-88.84, 20.55) * mm});
            skLineSegment(sketch, "E759", {"start": v(-88.84, 20.55) * mm, "end": v(-89.12, 20.47) * mm});
            skLineSegment(sketch, "E760", {"start": v(-89.12, 20.47) * mm, "end": v(-89.37, 20.34) * mm});
            skLineSegment(sketch, "E761", {"start": v(-89.37, 20.34) * mm, "end": v(-89.6, 20.15) * mm});
            skLineSegment(sketch, "E762", {"start": v(-89.6, 20.15) * mm, "end": v(-89.78, 19.92) * mm});
            skLineSegment(sketch, "E763", {"start": v(-89.78, 19.92) * mm, "end": v(-89.92, 19.67) * mm});
            skLineSegment(sketch, "E764", {"start": v(-89.92, 19.67) * mm, "end": v(-90, 19.4) * mm});
            skLineSegment(sketch, "E765", {"start": v(-90, 19.4) * mm, "end": v(-90, -30.22) * mm});
            skLineSegment(sketch, "E766", {"start": v(-90, -30.22) * mm, "end": v(-89.92, -30.5) * mm});
            skLineSegment(sketch, "E767", {"start": v(-89.92, -30.5) * mm, "end": v(-89.78, -30.74) * mm});
            skLineSegment(sketch, "E768", {"start": v(-89.78, -30.74) * mm, "end": v(-89.6, -30.97) * mm});
            skLineSegment(sketch, "E769", {"start": v(-89.6, -30.97) * mm, "end": v(-89.37, -31.16) * mm});
            skLineSegment(sketch, "E770", {"start": v(-89.37, -31.16) * mm, "end": v(-89.12, -31.3) * mm});
            skLineSegment(sketch, "E771", {"start": v(-89.12, -31.3) * mm, "end": v(-88.84, -31.37) * mm});
            skLineSegment(sketch, "E772", {"start": v(-88.84, -31.37) * mm, "end": v(-81.23, -31.37) * mm});
            skLineSegment(sketch, "E773", {"start": v(-81.23, -31.37) * mm, "end": v(-80.96, -31.3) * mm});
            skLineSegment(sketch, "E774", {"start": v(-80.96, -31.3) * mm, "end": v(-80.7, -31.16) * mm});
            skLineSegment(sketch, "E775", {"start": v(-80.7, -31.16) * mm, "end": v(-80.48, -30.97) * mm});
            skLineSegment(sketch, "E776", {"start": v(-80.48, -30.97) * mm, "end": v(-80.3, -30.74) * mm});
            skLineSegment(sketch, "E777", {"start": v(-80.3, -30.74) * mm, "end": v(-80.16, -30.5) * mm});
            skLineSegment(sketch, "E778", {"start": v(-80.16, -30.5) * mm, "end": v(-80.08, -30.22) * mm});
            skLineSegment(sketch, "E779", {"start": v(-80.08, -30.22) * mm, "end": v(-80.06, -10.46) * mm});
            skLineSegment(sketch, "E780", {"start": v(-80.06, -10.46) * mm, "end": v(-78.4, -10.46) * mm});
            skLineSegment(sketch, "E781", {"start": v(-78.4, -10.46) * mm, "end": v(-72.08, -30.59) * mm});
            skLineSegment(sketch, "E782", {"start": v(-72.08, -30.59) * mm, "end": v(-71.96, -30.79) * mm});
            skLineSegment(sketch, "E783", {"start": v(-71.96, -30.79) * mm, "end": v(-71.8, -30.96) * mm});
            skLineSegment(sketch, "E784", {"start": v(-71.8, -30.96) * mm, "end": v(-71.42, -31.24) * mm});
            skLineSegment(sketch, "E785", {"start": v(-71.42, -31.24) * mm, "end": v(-71.22, -31.33) * mm});
            skLineSegment(sketch, "E786", {"start": v(-71.22, -31.33) * mm, "end": v(-71, -31.38) * mm});
            skLineSegment(sketch, "E787", {"start": v(-71, -31.38) * mm, "end": v(-62.87, -31.33) * mm});
            skLineSegment(sketch, "E788", {"start": v(-62.87, -31.33) * mm, "end": v(-62.45, -31.12) * mm});
            skLineSegment(sketch, "E789", {"start": v(-62.45, -31.12) * mm, "end": v(-62.28, -30.96) * mm});
            skLineSegment(sketch, "E790", {"start": v(-62.28, -30.96) * mm, "end": v(-62.13, -30.79) * mm});
            skLineSegment(sketch, "E791", {"start": v(-62.13, -30.79) * mm, "end": v(-62.02, -30.59) * mm});
            skLineSegment(sketch, "E792", {"start": v(-62.02, -30.59) * mm, "end": v(-61.87, -30.14) * mm});
            skLineSegment(sketch, "E793", {"start": v(-61.87, -30.14) * mm, "end": v(-61.86, -29.9) * mm});
            skLineSegment(sketch, "E794", {"start": v(-61.86, -29.9) * mm, "end": v(-61.88, -29.68) * mm});
            skLineSegment(sketch, "E795", {"start": v(-73.77, 8.9) * mm, "end": v(-74.19, 9.74) * mm});
            skLineSegment(sketch, "E796", {"start": v(-74.19, 9.74) * mm, "end": v(-74.67, 10.27) * mm});
            skLineSegment(sketch, "E797", {"start": v(-74.67, 10.27) * mm, "end": v(-75.3, 10.64) * mm});
            skLineSegment(sketch, "E798", {"start": v(-75.3, 10.64) * mm, "end": v(-76.45, 10.94) * mm});
            skLineSegment(sketch, "E799", {"start": v(-76.45, 10.94) * mm, "end": v(-80.06, 11.03) * mm});
            skLineSegment(sketch, "E800", {"start": v(-80.06, 11.03) * mm, "end": v(-80.06, -1.3) * mm});
            skLineSegment(sketch, "E801", {"start": v(-80.06, -1.3) * mm, "end": v(-76.2, -1.22) * mm});
            skLineSegment(sketch, "E802", {"start": v(-76.2, -1.22) * mm, "end": v(-75.17, -0.94) * mm});
            skLineSegment(sketch, "E803", {"start": v(-75.17, -0.94) * mm, "end": v(-74.58, -0.55) * mm});
            skLineSegment(sketch, "E804", {"start": v(-74.58, -0.55) * mm, "end": v(-74.14, -0.04) * mm});
            skLineSegment(sketch, "E805", {"start": v(-74.14, -0.04) * mm, "end": v(-73.76, 0.8) * mm});
            skLineSegment(sketch, "E806", {"start": v(-73.76, 0.8) * mm, "end": v(-73.53, 1.77) * mm});
            skLineSegment(sketch, "E807", {"start": v(-73.53, 1.77) * mm, "end": v(-73.53, 7.94) * mm});
            skLineSegment(sketch, "E808", {"start": v(-73.53, 7.94) * mm, "end": v(-73.77, 8.9) * mm});
            skLineSegment(sketch, "E809", {"start": v(-30.26, 1.41) * mm, "end": v(-30.05, 1.26) * mm});
            skLineSegment(sketch, "E810", {"start": v(-30.05, 1.26) * mm, "end": v(-29.82, 1.17) * mm});
            skLineSegment(sketch, "E811", {"start": v(-29.82, 1.17) * mm, "end": v(-29.58, 1.12) * mm});
            skLineSegment(sketch, "E812", {"start": v(-29.58, 1.12) * mm, "end": v(-28.74, 1.13) * mm});
            skLineSegment(sketch, "E813", {"start": v(-28.74, 1.13) * mm, "end": v(-28.5, 1.06) * mm});
            skLineSegment(sketch, "E814", {"start": v(-28.5, 1.06) * mm, "end": v(-28.3, 0.95) * mm});
            skLineSegment(sketch, "E815", {"start": v(-28.3, 0.95) * mm, "end": v(-28.1, 0.8) * mm});
            skLineSegment(sketch, "E816", {"start": v(-28.1, 0.8) * mm, "end": v(-27.93, 0.6) * mm});
            skLineSegment(sketch, "E817", {"start": v(-27.93, 0.6) * mm, "end": v(-27.8, 0.35) * mm});
            skLineSegment(sketch, "E818", {"start": v(-27.8, 0.35) * mm, "end": v(-27.74, 0.1) * mm});
            skLineSegment(sketch, "E819", {"start": v(-27.74, 0.1) * mm, "end": v(-27.44, -3.69) * mm});
            skLineSegment(sketch, "E820", {"start": v(-27.44, -3.69) * mm, "end": v(-18.58, -3.69) * mm});
            skLineSegment(sketch, "E821", {"start": v(-18.58, -3.69) * mm, "end": v(-19.08, 0.94) * mm});
            skLineSegment(sketch, "E822", {"start": v(-19.08, 0.94) * mm, "end": v(-19.06, 1.2) * mm});
            skLineSegment(sketch, "E823", {"start": v(-19.06, 1.2) * mm, "end": v(-18.98, 1.46) * mm});
            skLineSegment(sketch, "E824", {"start": v(-18.98, 1.46) * mm, "end": v(-18.85, 1.7) * mm});
            skLineSegment(sketch, "E825", {"start": v(-18.85, 1.7) * mm, "end": v(-18.67, 1.9) * mm});
            skLineSegment(sketch, "E826", {"start": v(-18.67, 1.9) * mm, "end": v(-18.45, 2.05) * mm});
            skLineSegment(sketch, "E827", {"start": v(-18.45, 2.05) * mm, "end": v(-18.2, 2.16) * mm});
            skLineSegment(sketch, "E828", {"start": v(-18.2, 2.16) * mm, "end": v(-17.47, 2.28) * mm});
            skLineSegment(sketch, "E829", {"start": v(-17.47, 2.28) * mm, "end": v(-17.24, 2.37) * mm});
            skLineSegment(sketch, "E830", {"start": v(-17.24, 2.37) * mm, "end": v(-17.04, 2.5) * mm});
            skLineSegment(sketch, "E831", {"start": v(-17.04, 2.5) * mm, "end": v(-16.86, 2.7) * mm});
            skLineSegment(sketch, "E832", {"start": v(-16.86, 2.7) * mm, "end": v(-16.71, 2.9) * mm});
            skLineSegment(sketch, "E833", {"start": v(-16.71, 2.9) * mm, "end": v(-16.61, 3.13) * mm});
            skLineSegment(sketch, "E834", {"start": v(-16.61, 3.13) * mm, "end": v(-16.57, 3.37) * mm});
            skLineSegment(sketch, "E835", {"start": v(-16.57, 3.37) * mm, "end": v(-16.57, 3.63) * mm});
            skLineSegment(sketch, "E836", {"start": v(-16.57, 3.63) * mm, "end": v(-16.62, 3.89) * mm});
            skLineSegment(sketch, "E837", {"start": v(-16.62, 3.89) * mm, "end": v(-16.7, 4.11) * mm});
            skLineSegment(sketch, "E838", {"start": v(-16.7, 4.11) * mm, "end": v(-16.85, 4.32) * mm});
            skLineSegment(sketch, "E839", {"start": v(-16.85, 4.32) * mm, "end": v(-17.03, 4.5) * mm});
            skLineSegment(sketch, "E840", {"start": v(-17.03, 4.5) * mm, "end": v(-17.25, 4.65) * mm});
            skLineSegment(sketch, "E841", {"start": v(-17.25, 4.65) * mm, "end": v(-17.47, 4.74) * mm});
            skLineSegment(sketch, "E842", {"start": v(-17.47, 4.74) * mm, "end": v(-17.7, 4.79) * mm});
            skLineSegment(sketch, "E843", {"start": v(-17.7, 4.79) * mm, "end": v(-29.82, 3.62) * mm});
            skLineSegment(sketch, "E844", {"start": v(-29.82, 3.62) * mm, "end": v(-30.05, 3.53) * mm});
            skLineSegment(sketch, "E845", {"start": v(-30.05, 3.53) * mm, "end": v(-30.25, 3.4) * mm});
            skLineSegment(sketch, "E846", {"start": v(-30.25, 3.4) * mm, "end": v(-30.44, 3.21) * mm});
            skLineSegment(sketch, "E847", {"start": v(-30.44, 3.21) * mm, "end": v(-30.58, 3) * mm});
            skLineSegment(sketch, "E848", {"start": v(-30.58, 3) * mm, "end": v(-30.67, 2.78) * mm});
            skLineSegment(sketch, "E849", {"start": v(-30.67, 2.78) * mm, "end": v(-30.72, 2.54) * mm});
            skLineSegment(sketch, "E850", {"start": v(-30.72, 2.54) * mm, "end": v(-30.72, 2.27) * mm});
            skLineSegment(sketch, "E851", {"start": v(-30.72, 2.27) * mm, "end": v(-30.67, 2.02) * mm});
            skLineSegment(sketch, "E852", {"start": v(-30.67, 2.02) * mm, "end": v(-30.58, 1.8) * mm});
            skLineSegment(sketch, "E853", {"start": v(-30.58, 1.8) * mm, "end": v(-30.45, 1.6) * mm});
            skLineSegment(sketch, "E854", {"start": v(-30.45, 1.6) * mm, "end": v(-30.26, 1.41) * mm});
            skLineSegment(sketch, "E855.bottom", {"start": v(-97.2, 35.98) * mm, "end": v(95.68, 35.98) * mm});
            skLineSegment(sketch, "E855.top", {"start": v(-97.2, -37.18) * mm, "end": v(95.68, -37.18) * mm});
            skLineSegment(sketch, "E855.left", {"start": v(-97.2, 35.98) * mm, "end": v(-97.2, -37.18) * mm});
            skLineSegment(sketch, "E855.right", {"start": v(95.68, 35.98) * mm, "end": v(95.68, -37.18) * mm});
            skSolve(sketch);
        }
        {
            var Q0;
            Q0=qCreatedBy(makeId("Top.planeOp"),FACE);
            var sketch = newSketch(context, id + "F1", { "sketchPlane" : qUnion([Q0])});
            skLineSegment(sketch, "E856.0", {"start": v(-97.2, 35.98) * mm, "end": v(95.68, 35.98) * mm});
            skLineSegment(sketch, "E856.1", {"start": v(95.68, 35.98) * mm, "end": v(95.68, -37.18) * mm});
            skLineSegment(sketch, "E856.2", {"start": v(-97.2, -37.18) * mm, "end": v(95.68, -37.18) * mm});
            skLineSegment(sketch, "E856.3", {"start": v(-97.2, 35.98) * mm, "end": v(-97.2, -37.18) * mm});
            skSolve(sketch);
        }
        {
            var Q0;
            Q0=qSketchRegion(id+"F1",true);
            extrude(context, id + "F2", {"entities" : qUnion([Q0]), "depth" : .3 * mm});
        }
        {
            var Q0;
            Q0=makeQuery(id+"F0.imprint","IMPRINT",FACE,{"disambiguationData":[TD([[makeQuery(id+"F0.imprint","IMPRINT",EDGE,{"derivedFrom":sQuery(id+"F0.wireOp",EDGE,"E0")}),1.0]])]});
            var Q1;
            Q1=makeQuery(id+"F0.imprint","IMPRINT",FACE,{"disambiguationData":[TD([[makeQuery(id+"F0.imprint","IMPRINT",EDGE,{"derivedFrom":sQuery(id+"F0.wireOp",EDGE,"E795")}),1.0]])]});
            var Q2;
            Q2=makeQuery(id+"F0.imprint","IMPRINT",FACE,{"disambiguationData":[TD([[makeQuery(id+"F0.imprint","IMPRINT",EDGE,{"derivedFrom":sQuery(id+"F0.wireOp",EDGE,"E809")}),1.0]])]});
            var Q3;
            Q3=makeQuery(id+"F0.imprint","IMPRINT",FACE,{"disambiguationData":[TD([[makeQuery(id+"F0.imprint","IMPRINT",EDGE,{"derivedFrom":sQuery(id+"F0.wireOp",EDGE,"E107")}),1.0]])]});
            var Q4;
            Q4=makeQuery(id+"F0.imprint","IMPRINT",FACE,{"disambiguationData":[TD([[makeQuery(id+"F0.imprint","IMPRINT",EDGE,{"derivedFrom":sQuery(id+"F0.wireOp",EDGE,"E75")}),1.0]])]});
            var Q5;
            Q5=makeQuery(id+"F0.imprint","IMPRINT",FACE,{"disambiguationData":[TD([[makeQuery(id+"F0.imprint","IMPRINT",EDGE,{"derivedFrom":sQuery(id+"F0.wireOp",EDGE,"E43")}),1.0]])]});
            var Q6;
            Q6=makeQuery(id+"F0.imprint","IMPRINT",FACE,{"disambiguationData":[TD([[makeQuery(id+"F0.imprint","IMPRINT",EDGE,{"derivedFrom":sQuery(id+"F0.wireOp",EDGE,"E672")}),1.0]])]});
            var Q7;
            Q7=makeQuery(id+"F0.imprint","IMPRINT",FACE,{"disambiguationData":[TD([[makeQuery(id+"F0.imprint","IMPRINT",EDGE,{"derivedFrom":sQuery(id+"F0.wireOp",EDGE,"E582")}),1.0]])]});
            var Q8;
            Q8=makeQuery(id+"F0.imprint","IMPRINT",FACE,{"disambiguationData":[TD([[makeQuery(id+"F0.imprint","IMPRINT",EDGE,{"derivedFrom":sQuery(id+"F0.wireOp",EDGE,"E598")}),1.0]])]});
            extrude(context, id + "F3", {"entities" : qUnion([Q0, Q1, Q2, Q3, Q4, Q5, Q6, Q7, Q8]), "operationType" : NewBodyOperationType.REMOVE, "depth" : .3 * mm});
        }
        {
            var Q0;
            Q0=qCreatedBy(makeId("Top.planeOp"),FACE);
            var sketch = newSketch(context, id + "F4", { "sketchPlane" : qUnion([Q0])});
            skCircle(sketch, "E857", {"center": v(-24.76, 19.55) * mm, "radius": 9.16 * mm});
            skCircle(sketch, "E858", {"center": v(-24.76, 19.55) * mm, "radius": 8.22 * mm});
            skLineSegment(sketch, "E859.bottom", {"start": v(-65.3, -26.87) * mm, "end": v(72.64, -26.87) * mm});
            skLineSegment(sketch, "E859.top", {"start": v(-65.3, -27.83) * mm, "end": v(72.64, -27.83) * mm});
            skLineSegment(sketch, "E859.left", {"start": v(-65.3, -26.87) * mm, "end": v(-65.3, -27.83) * mm});
            skLineSegment(sketch, "E859.right", {"start": v(72.64, -26.87) * mm, "end": v(72.64, -27.83) * mm});
            skLineSegment(sketch, "E860.bottom", {"start": v(-15.53, 4.55) * mm, "end": v(75.82, 4.55) * mm});
            skLineSegment(sketch, "E860.top", {"start": v(-15.53, 3.14) * mm, "end": v(75.82, 3.14) * mm});
            skLineSegment(sketch, "E860.left", {"start": v(-15.53, 4.55) * mm, "end": v(-15.53, 3.14) * mm});
            skLineSegment(sketch, "E860.right", {"start": v(75.82, 4.55) * mm, "end": v(75.82, 3.14) * mm});
            skLineSegment(sketch, "E861.bottom", {"start": v(-32.09, 3.14) * mm, "end": v(-64.5, 3.14) * mm});
            skLineSegment(sketch, "E861.top", {"start": v(-32.09, 2) * mm, "end": v(-64.5, 2) * mm});
            skLineSegment(sketch, "E861.left", {"start": v(-32.09, 3.14) * mm, "end": v(-32.09, 2) * mm});
            skLineSegment(sketch, "E861.right", {"start": v(-64.5, 3.14) * mm, "end": v(-64.5, 2) * mm});
            skLineSegment(sketch, "E862.bottom", {"start": v(-68.44, 16.93) * mm, "end": v(-32.85, 16.93) * mm});
            skLineSegment(sketch, "E862.top", {"start": v(-68.44, 18.06) * mm, "end": v(-32.85, 18.06) * mm});
            skLineSegment(sketch, "E862.left", {"start": v(-68.44, 16.93) * mm, "end": v(-68.44, 18.06) * mm});
            skLineSegment(sketch, "E862.right", {"start": v(-32.85, 16.93) * mm, "end": v(-32.85, 18.06) * mm});
            skLineSegment(sketch, "E863.bottom", {"start": v(-24.5, 12.33) * mm, "end": v(-23.54, 12.33) * mm});
            skLineSegment(sketch, "E863.top", {"start": v(-24.5, 5.3) * mm, "end": v(-23.54, 5.3) * mm});
            skLineSegment(sketch, "E863.left", {"start": v(-24.5, 12.33) * mm, "end": v(-24.5, 5.3) * mm});
            skLineSegment(sketch, "E863.right", {"start": v(-23.54, 12.33) * mm, "end": v(-23.54, 5.3) * mm});
            skSolve(sketch);
        }
        {
            var Q0;
            Q0=qSketchRegion(id+"F4",true);
            extrude(context, id + "F5", {"entities" : qUnion([Q0]), "operationType" : NewBodyOperationType.ADD, "depth" : .1 * mm});
        }
    });
